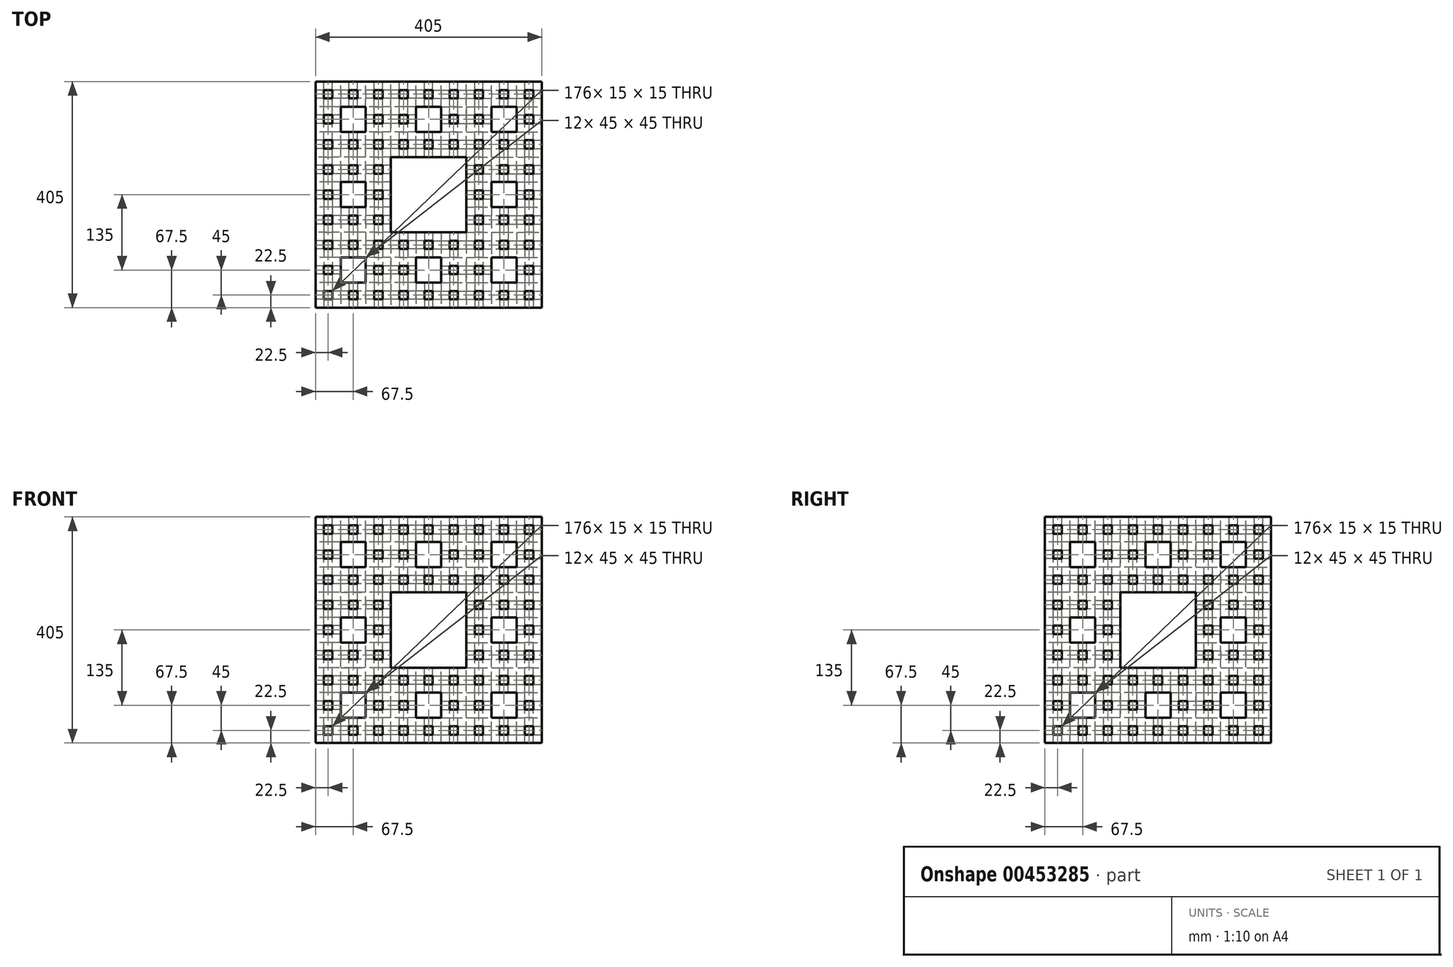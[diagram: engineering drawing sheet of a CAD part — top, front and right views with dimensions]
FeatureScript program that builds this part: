
annotation { "Feature Type Name" : "Feature", "Feature Type Description" : "" }
export const myFeature = defineFeature(function(context is Context, id is Id, definition is map)
    precondition{}
    {
        {
            var Q0;
            Q0=qCreatedBy(makeId("Top.planeOp"),FACE);
            var sketch = newSketch(context, id + "F0", { "sketchPlane" : qUnion([Q0])});
            skLineSegment(sketch, "E0.bottom", {"start": v(-202.5, 101.25) * mm, "end": v(0, 101.25) * mm});
            skLineSegment(sketch, "E0.top", {"start": v(-202.5, -101.25) * mm, "end": v(0, -101.25) * mm});
            skLineSegment(sketch, "E0.left", {"start": v(-202.5, 101.25) * mm, "end": v(-202.5, -101.25) * mm});
            skLineSegment(sketch, "E0.right", {"start": v(0, 101.25) * mm, "end": v(0, -101.25) * mm});
            skPoint(sketch, "E0.middle", {"position": v(-101.25, 0) * mm});
            skSolve(sketch);
        }
        {
            var Q0;
            Q0=makeQuery(id+"F0.imprint","IMPRINT",FACE,{"disambiguationData":[TD([[makeQuery(id+"F0.imprint","IMPRINT",EDGE,{"derivedFrom":sQuery(id+"F0.wireOp",EDGE,"E0.bottom")}),-1.0]])]});
            extrude(context, id + "F1", {"entities" : qUnion([Q0]), "depth" : 405 * mm});
        }
        {
            var Q0;
            Q0=makeQuery(id+"F1.opExtrude","SWEPT_FACE",FACE,{"disambiguationData":[OSD([sQuery(id+"F0.wireOp",EDGE,"E0.left")])]});
            var sketch = newSketch(context, id + "F2", { "sketchPlane" : qUnion([Q0])});
            skLineSegment(sketch, "E1.bottom", {"start": v(33.75, 270) * mm, "end": v(168.75, 270) * mm});
            skLineSegment(sketch, "E1.top", {"start": v(33.75, 135) * mm, "end": v(168.75, 135) * mm});
            skLineSegment(sketch, "E1.left", {"start": v(33.75, 270) * mm, "end": v(33.75, 135) * mm});
            skLineSegment(sketch, "E1.right", {"start": v(168.75, 270) * mm, "end": v(168.75, 135) * mm});
            skPoint(sketch, "E1.middle", {"position": v(101.25, 202.5) * mm});
            skSolve(sketch);
        }
        {
            var Q0;
            Q0=qSketchRegion(id+"F2",true);
            extrude(context, id + "F3", {"entities" : qUnion([Q0]), "operationType" : NewBodyOperationType.REMOVE, "oppositeDirection" : true, "depth" : 1000 * mm});
        }
        {
            var Q0;
            Q0=makeQuery(id+"F1.opExtrude","SWEPT_FACE",FACE,{"disambiguationData":[OSD([sQuery(id+"F0.wireOp",EDGE,"E0.left")])]});
            var sketch = newSketch(context, id + "F4", { "sketchPlane" : qUnion([Q0])});
            skLineSegment(sketch, "E2.bottom", {"start": v(-56.25, 360) * mm, "end": v(-11.25, 360) * mm});
            skLineSegment(sketch, "E2.top", {"start": v(-56.25, 315) * mm, "end": v(-11.25, 315) * mm});
            skLineSegment(sketch, "E2.left", {"start": v(-56.25, 360) * mm, "end": v(-56.25, 315) * mm});
            skLineSegment(sketch, "E2.right", {"start": v(-11.25, 360) * mm, "end": v(-11.25, 315) * mm});
            skPoint(sketch, "E2.middle", {"position": v(-33.75, 337.5) * mm});
            skLineSegment(sketch, "E3.bottom", {"start": v(78.75, 360) * mm, "end": v(123.75, 360) * mm});
            skLineSegment(sketch, "E3.top", {"start": v(78.75, 315) * mm, "end": v(123.75, 315) * mm});
            skLineSegment(sketch, "E3.left", {"start": v(78.75, 360) * mm, "end": v(78.75, 315) * mm});
            skLineSegment(sketch, "E3.right", {"start": v(123.75, 360) * mm, "end": v(123.75, 315) * mm});
            skPoint(sketch, "E3.middle", {"position": v(101.25, 337.5) * mm});
            skLineSegment(sketch, "E4.bottom", {"start": v(-56.25, 225) * mm, "end": v(-11.25, 225) * mm});
            skLineSegment(sketch, "E4.top", {"start": v(-56.25, 180) * mm, "end": v(-11.25, 180) * mm});
            skLineSegment(sketch, "E4.left", {"start": v(-56.25, 225) * mm, "end": v(-56.25, 180) * mm});
            skLineSegment(sketch, "E4.right", {"start": v(-11.25, 225) * mm, "end": v(-11.25, 180) * mm});
            skPoint(sketch, "E4.middle", {"position": v(-33.75, 202.5) * mm});
            skLineSegment(sketch, "E5.bottom", {"start": v(-56.25, 90) * mm, "end": v(-11.25, 90) * mm});
            skLineSegment(sketch, "E5.top", {"start": v(-56.25, 45) * mm, "end": v(-11.25, 45) * mm});
            skLineSegment(sketch, "E5.left", {"start": v(-56.25, 90) * mm, "end": v(-56.25, 45) * mm});
            skLineSegment(sketch, "E5.right", {"start": v(-11.25, 90) * mm, "end": v(-11.25, 45) * mm});
            skPoint(sketch, "E5.middle", {"position": v(-33.75, 67.5) * mm});
            skLineSegment(sketch, "E6.bottom", {"start": v(78.75, 90) * mm, "end": v(123.75, 90) * mm});
            skLineSegment(sketch, "E6.top", {"start": v(78.75, 45) * mm, "end": v(123.75, 45) * mm});
            skLineSegment(sketch, "E6.left", {"start": v(78.75, 90) * mm, "end": v(78.75, 45) * mm});
            skLineSegment(sketch, "E6.right", {"start": v(123.75, 90) * mm, "end": v(123.75, 45) * mm});
            skPoint(sketch, "E6.middle", {"position": v(101.25, 67.5) * mm});
            skSolve(sketch);
        }
        {
            var Q0;
            Q0=qSketchRegion(id+"F4",true);
            extrude(context, id + "F5", {"entities" : qUnion([Q0]), "operationType" : NewBodyOperationType.REMOVE, "oppositeDirection" : true, "depth" : 1000 * mm});
        }
        {
            var Q0;
            Q0=makeQuery(id+"F1.opExtrude","SWEPT_FACE",FACE,{"disambiguationData":[OSD([sQuery(id+"F0.wireOp",EDGE,"E0.left")])]});
            var sketch = newSketch(context, id + "F6", { "sketchPlane" : qUnion([Q0])});
            skLineSegment(sketch, "E7.bottom", {"start": v(-71.25, 390) * mm, "end": v(-86.25, 390) * mm});
            skLineSegment(sketch, "E7.top", {"start": v(-71.25, 375) * mm, "end": v(-86.25, 375) * mm});
            skLineSegment(sketch, "E7.left", {"start": v(-71.25, 390) * mm, "end": v(-71.25, 375) * mm});
            skLineSegment(sketch, "E7.right", {"start": v(-86.25, 390) * mm, "end": v(-86.25, 375) * mm});
            skPoint(sketch, "E7.middle", {"position": v(-78.75, 382.5) * mm});
            skLineSegment(sketch, "E8.bottom", {"start": v(-26.25, 390) * mm, "end": v(-41.25, 390) * mm});
            skLineSegment(sketch, "E8.top", {"start": v(-26.25, 375) * mm, "end": v(-41.25, 375) * mm});
            skLineSegment(sketch, "E8.left", {"start": v(-26.25, 390) * mm, "end": v(-26.25, 375) * mm});
            skLineSegment(sketch, "E8.right", {"start": v(-41.25, 390) * mm, "end": v(-41.25, 375) * mm});
            skPoint(sketch, "E8.middle", {"position": v(-33.75, 382.5) * mm});
            skLineSegment(sketch, "E9.bottom", {"start": v(18.75, 375) * mm, "end": v(3.75, 375) * mm});
            skLineSegment(sketch, "E9.top", {"start": v(18.75, 390) * mm, "end": v(3.75, 390) * mm});
            skLineSegment(sketch, "E9.left", {"start": v(18.75, 375) * mm, "end": v(18.75, 390) * mm});
            skLineSegment(sketch, "E9.right", {"start": v(3.75, 375) * mm, "end": v(3.75, 390) * mm});
            skPoint(sketch, "E9.middle", {"position": v(11.25, 382.5) * mm});
            skLineSegment(sketch, "E10.bottom", {"start": v(63.75, 375) * mm, "end": v(48.75, 375) * mm});
            skLineSegment(sketch, "E10.top", {"start": v(63.75, 390) * mm, "end": v(48.75, 390) * mm});
            skLineSegment(sketch, "E10.left", {"start": v(63.75, 375) * mm, "end": v(63.75, 390) * mm});
            skLineSegment(sketch, "E10.right", {"start": v(48.75, 375) * mm, "end": v(48.75, 390) * mm});
            skPoint(sketch, "E10.middle", {"position": v(56.25, 382.5) * mm});
            skLineSegment(sketch, "E11.bottom", {"start": v(93.75, 390) * mm, "end": v(108.75, 390) * mm});
            skLineSegment(sketch, "E11.top", {"start": v(93.75, 375) * mm, "end": v(108.75, 375) * mm});
            skLineSegment(sketch, "E11.left", {"start": v(93.75, 390) * mm, "end": v(93.75, 375) * mm});
            skLineSegment(sketch, "E11.right", {"start": v(108.75, 390) * mm, "end": v(108.75, 375) * mm});
            skPoint(sketch, "E11.middle", {"position": v(101.25, 382.5) * mm});
            skLineSegment(sketch, "E12.bottom", {"start": v(-86.25, 345) * mm, "end": v(-71.25, 345) * mm});
            skLineSegment(sketch, "E12.top", {"start": v(-86.25, 330) * mm, "end": v(-71.25, 330) * mm});
            skLineSegment(sketch, "E12.left", {"start": v(-86.25, 345) * mm, "end": v(-86.25, 330) * mm});
            skLineSegment(sketch, "E12.right", {"start": v(-71.25, 345) * mm, "end": v(-71.25, 330) * mm});
            skPoint(sketch, "E12.middle", {"position": v(-78.75, 337.5) * mm});
            skLineSegment(sketch, "E13.bottom", {"start": v(-86.25, 300) * mm, "end": v(-71.25, 300) * mm});
            skLineSegment(sketch, "E13.top", {"start": v(-86.25, 285) * mm, "end": v(-71.25, 285) * mm});
            skLineSegment(sketch, "E13.left", {"start": v(-86.25, 300) * mm, "end": v(-86.25, 285) * mm});
            skLineSegment(sketch, "E13.right", {"start": v(-71.25, 300) * mm, "end": v(-71.25, 285) * mm});
            skPoint(sketch, "E13.middle", {"position": v(-78.75, 292.5) * mm});
            skLineSegment(sketch, "E14.bottom", {"start": v(-86.25, 255) * mm, "end": v(-71.25, 255) * mm});
            skLineSegment(sketch, "E14.top", {"start": v(-86.25, 240) * mm, "end": v(-71.25, 240) * mm});
            skLineSegment(sketch, "E14.left", {"start": v(-86.25, 255) * mm, "end": v(-86.25, 240) * mm});
            skLineSegment(sketch, "E14.right", {"start": v(-71.25, 255) * mm, "end": v(-71.25, 240) * mm});
            skPoint(sketch, "E14.middle", {"position": v(-78.75, 247.5) * mm});
            skLineSegment(sketch, "E15.bottom", {"start": v(-86.25, 210) * mm, "end": v(-71.25, 210) * mm});
            skLineSegment(sketch, "E15.top", {"start": v(-86.25, 195) * mm, "end": v(-71.25, 195) * mm});
            skLineSegment(sketch, "E15.left", {"start": v(-86.25, 210) * mm, "end": v(-86.25, 195) * mm});
            skLineSegment(sketch, "E15.right", {"start": v(-71.25, 210) * mm, "end": v(-71.25, 195) * mm});
            skPoint(sketch, "E15.middle", {"position": v(-78.75, 202.5) * mm});
            skLineSegment(sketch, "E16.bottom", {"start": v(-86.25, 165) * mm, "end": v(-71.25, 165) * mm});
            skLineSegment(sketch, "E16.top", {"start": v(-86.25, 150) * mm, "end": v(-71.25, 150) * mm});
            skLineSegment(sketch, "E16.left", {"start": v(-86.25, 165) * mm, "end": v(-86.25, 150) * mm});
            skLineSegment(sketch, "E16.right", {"start": v(-71.25, 165) * mm, "end": v(-71.25, 150) * mm});
            skPoint(sketch, "E16.middle", {"position": v(-78.75, 157.5) * mm});
            skLineSegment(sketch, "E17.bottom", {"start": v(-86.25, 105) * mm, "end": v(-71.25, 105) * mm});
            skLineSegment(sketch, "E17.top", {"start": v(-86.25, 120) * mm, "end": v(-71.25, 120) * mm});
            skLineSegment(sketch, "E17.left", {"start": v(-86.25, 105) * mm, "end": v(-86.25, 120) * mm});
            skLineSegment(sketch, "E17.right", {"start": v(-71.25, 105) * mm, "end": v(-71.25, 120) * mm});
            skPoint(sketch, "E17.middle", {"position": v(-78.75, 112.5) * mm});
            skLineSegment(sketch, "E18.bottom", {"start": v(-86.25, 75) * mm, "end": v(-71.25, 75) * mm});
            skLineSegment(sketch, "E18.top", {"start": v(-86.25, 60) * mm, "end": v(-71.25, 60) * mm});
            skLineSegment(sketch, "E18.left", {"start": v(-86.25, 75) * mm, "end": v(-86.25, 60) * mm});
            skLineSegment(sketch, "E18.right", {"start": v(-71.25, 75) * mm, "end": v(-71.25, 60) * mm});
            skPoint(sketch, "E18.middle", {"position": v(-78.75, 67.5) * mm});
            skLineSegment(sketch, "E19.bottom", {"start": v(-86.25, 15) * mm, "end": v(-71.25, 15) * mm});
            skLineSegment(sketch, "E19.top", {"start": v(-86.25, 30) * mm, "end": v(-71.25, 30) * mm});
            skLineSegment(sketch, "E19.left", {"start": v(-86.25, 15) * mm, "end": v(-86.25, 30) * mm});
            skLineSegment(sketch, "E19.right", {"start": v(-71.25, 15) * mm, "end": v(-71.25, 30) * mm});
            skPoint(sketch, "E19.middle", {"position": v(-78.75, 22.5) * mm});
            skLineSegment(sketch, "E20", {"start": v(108.75, 390) * mm, "end": v(-86.25, 390) * mm, "construction": true});
            skLineSegment(sketch, "E21", {"start": v(-86.25, 390) * mm, "end": v(-86.25, -15.3) * mm, "construction": true});
            skLineSegment(sketch, "E22.bottom", {"start": v(-26.25, 30) * mm, "end": v(-41.25, 30) * mm});
            skLineSegment(sketch, "E22.top", {"start": v(-26.25, 15) * mm, "end": v(-41.25, 15) * mm});
            skLineSegment(sketch, "E22.left", {"start": v(-26.25, 30) * mm, "end": v(-26.25, 15) * mm});
            skLineSegment(sketch, "E22.right", {"start": v(-41.25, 30) * mm, "end": v(-41.25, 15) * mm});
            skPoint(sketch, "E22.middle", {"position": v(-33.75, 22.5) * mm});
            skLineSegment(sketch, "E23.bottom", {"start": v(18.75, 30) * mm, "end": v(3.75, 30) * mm});
            skLineSegment(sketch, "E23.top", {"start": v(18.75, 15) * mm, "end": v(3.75, 15) * mm});
            skLineSegment(sketch, "E23.left", {"start": v(18.75, 30) * mm, "end": v(18.75, 15) * mm});
            skLineSegment(sketch, "E23.right", {"start": v(3.75, 30) * mm, "end": v(3.75, 15) * mm});
            skPoint(sketch, "E23.middle", {"position": v(11.25, 22.5) * mm});
            skLineSegment(sketch, "E24.bottom", {"start": v(63.75, 30) * mm, "end": v(48.75, 30) * mm});
            skLineSegment(sketch, "E24.top", {"start": v(63.75, 15) * mm, "end": v(48.75, 15) * mm});
            skLineSegment(sketch, "E24.left", {"start": v(63.75, 30) * mm, "end": v(63.75, 15) * mm});
            skLineSegment(sketch, "E24.right", {"start": v(48.75, 30) * mm, "end": v(48.75, 15) * mm});
            skPoint(sketch, "E24.middle", {"position": v(56.25, 22.5) * mm});
            skLineSegment(sketch, "E25.bottom", {"start": v(93.75, 30) * mm, "end": v(108.75, 30) * mm});
            skLineSegment(sketch, "E25.top", {"start": v(93.75, 15) * mm, "end": v(108.75, 15) * mm});
            skLineSegment(sketch, "E25.left", {"start": v(93.75, 30) * mm, "end": v(93.75, 15) * mm});
            skLineSegment(sketch, "E25.right", {"start": v(108.75, 30) * mm, "end": v(108.75, 15) * mm});
            skPoint(sketch, "E25.middle", {"position": v(101.25, 22.5) * mm});
            skLineSegment(sketch, "E26", {"start": v(108.75, 15) * mm, "end": v(-86.25, 15) * mm, "construction": true});
            skLineSegment(sketch, "E27.bottom", {"start": v(-41.25, 285) * mm, "end": v(-26.25, 285) * mm});
            skLineSegment(sketch, "E27.top", {"start": v(-41.25, 300) * mm, "end": v(-26.25, 300) * mm});
            skLineSegment(sketch, "E27.left", {"start": v(-41.25, 285) * mm, "end": v(-41.25, 300) * mm});
            skLineSegment(sketch, "E27.right", {"start": v(-26.25, 285) * mm, "end": v(-26.25, 300) * mm});
            skPoint(sketch, "E27.middle", {"position": v(-33.75, 292.5) * mm});
            skPoint(sketch, "E27.middle.positionSnap0", {"position": v(-33.75, 315) * mm});
            skPoint(sketch, "E27.centerSnap0", {"position": v(-33.75, 315) * mm});
            skLineSegment(sketch, "E28.bottom", {"start": v(-41.25, 240) * mm, "end": v(-26.25, 240) * mm});
            skLineSegment(sketch, "E28.top", {"start": v(-41.25, 255) * mm, "end": v(-26.25, 255) * mm});
            skLineSegment(sketch, "E28.left", {"start": v(-41.25, 240) * mm, "end": v(-41.25, 255) * mm});
            skLineSegment(sketch, "E28.right", {"start": v(-26.25, 240) * mm, "end": v(-26.25, 255) * mm});
            skPoint(sketch, "E28.middle", {"position": v(-33.75, 247.5) * mm});
            skLineSegment(sketch, "E29.bottom", {"start": v(18.75, 330) * mm, "end": v(3.75, 330) * mm});
            skLineSegment(sketch, "E29.top", {"start": v(18.75, 345) * mm, "end": v(3.75, 345) * mm});
            skLineSegment(sketch, "E29.left", {"start": v(18.75, 330) * mm, "end": v(18.75, 345) * mm});
            skLineSegment(sketch, "E29.right", {"start": v(3.75, 330) * mm, "end": v(3.75, 345) * mm});
            skPoint(sketch, "E29.middle", {"position": v(11.25, 337.5) * mm});
            skPoint(sketch, "E29.middle.positionSnap0", {"position": v(-11.25, 337.5) * mm});
            skPoint(sketch, "E29.centerSnap0", {"position": v(-11.25, 337.5) * mm});
            skLineSegment(sketch, "E30.bottom", {"start": v(48.75, 330) * mm, "end": v(63.75, 330) * mm});
            skLineSegment(sketch, "E30.top", {"start": v(48.75, 345) * mm, "end": v(63.75, 345) * mm});
            skLineSegment(sketch, "E30.left", {"start": v(48.75, 330) * mm, "end": v(48.75, 345) * mm});
            skLineSegment(sketch, "E30.right", {"start": v(63.75, 330) * mm, "end": v(63.75, 345) * mm});
            skPoint(sketch, "E30.middle", {"position": v(56.25, 337.5) * mm});
            skPoint(sketch, "E30.middle.positionSnap0", {"position": v(78.75, 337.5) * mm});
            skPoint(sketch, "E30.centerSnap0", {"position": v(78.75, 337.5) * mm});
            skLineSegment(sketch, "E31.bottom", {"start": v(-41.25, 150) * mm, "end": v(-26.25, 150) * mm});
            skLineSegment(sketch, "E31.top", {"start": v(-41.25, 165) * mm, "end": v(-26.25, 165) * mm});
            skLineSegment(sketch, "E31.left", {"start": v(-41.25, 150) * mm, "end": v(-41.25, 165) * mm});
            skLineSegment(sketch, "E31.right", {"start": v(-26.25, 150) * mm, "end": v(-26.25, 165) * mm});
            skPoint(sketch, "E31.middle", {"position": v(-33.75, 157.5) * mm});
            skPoint(sketch, "E31.middle.positionSnap0", {"position": v(-33.75, 180) * mm});
            skPoint(sketch, "E31.centerSnap0", {"position": v(-33.75, 180) * mm});
            skLineSegment(sketch, "E32.bottom", {"start": v(-41.25, 120) * mm, "end": v(-26.25, 120) * mm});
            skLineSegment(sketch, "E32.top", {"start": v(-41.25, 105) * mm, "end": v(-26.25, 105) * mm});
            skLineSegment(sketch, "E32.left", {"start": v(-41.25, 120) * mm, "end": v(-41.25, 105) * mm});
            skLineSegment(sketch, "E32.right", {"start": v(-26.25, 120) * mm, "end": v(-26.25, 105) * mm});
            skPoint(sketch, "E32.middle", {"position": v(-33.75, 112.5) * mm});
            skPoint(sketch, "E32.middle.positionSnap0", {"position": v(-33.75, 90) * mm});
            skPoint(sketch, "E32.centerSnap0", {"position": v(-33.75, 90) * mm});
            skLineSegment(sketch, "E33.bottom", {"start": v(18.75, 60) * mm, "end": v(3.75, 60) * mm});
            skLineSegment(sketch, "E33.top", {"start": v(18.75, 75) * mm, "end": v(3.75, 75) * mm});
            skLineSegment(sketch, "E33.left", {"start": v(18.75, 60) * mm, "end": v(18.75, 75) * mm});
            skLineSegment(sketch, "E33.right", {"start": v(3.75, 60) * mm, "end": v(3.75, 75) * mm});
            skPoint(sketch, "E33.middle", {"position": v(11.25, 67.5) * mm});
            skPoint(sketch, "E33.middle.positionSnap0", {"position": v(11.25, 30) * mm});
            skPoint(sketch, "E33.middle.positionSnap1", {"position": v(-11.25, 67.5) * mm});
            skPoint(sketch, "E33.centerSnap0", {"position": v(11.25, 30) * mm});
            skPoint(sketch, "E33.centerSnap1", {"position": v(-11.25, 67.5) * mm});
            skLineSegment(sketch, "E34.bottom", {"start": v(48.75, 75) * mm, "end": v(63.75, 75) * mm});
            skLineSegment(sketch, "E34.top", {"start": v(48.75, 60) * mm, "end": v(63.75, 60) * mm});
            skLineSegment(sketch, "E34.left", {"start": v(48.75, 75) * mm, "end": v(48.75, 60) * mm});
            skLineSegment(sketch, "E34.right", {"start": v(63.75, 75) * mm, "end": v(63.75, 60) * mm});
            skPoint(sketch, "E34.middle", {"position": v(56.25, 67.5) * mm});
            skPoint(sketch, "E34.middle.positionSnap0", {"position": v(78.75, 67.5) * mm});
            skPoint(sketch, "E34.middle.positionSnap1", {"position": v(56.25, 30) * mm});
            skPoint(sketch, "E34.centerSnap0", {"position": v(78.75, 67.5) * mm});
            skPoint(sketch, "E34.centerSnap1", {"position": v(56.25, 30) * mm});
            skLineSegment(sketch, "E35.bottom", {"start": v(3.75, 300) * mm, "end": v(18.75, 300) * mm});
            skLineSegment(sketch, "E35.top", {"start": v(3.75, 285) * mm, "end": v(18.75, 285) * mm});
            skLineSegment(sketch, "E35.left", {"start": v(3.75, 300) * mm, "end": v(3.75, 285) * mm});
            skLineSegment(sketch, "E35.right", {"start": v(18.75, 300) * mm, "end": v(18.75, 285) * mm});
            skPoint(sketch, "E35.middle", {"position": v(11.25, 292.5) * mm});
            skPoint(sketch, "E35.middle.positionSnap0", {"position": v(-26.25, 292.5) * mm});
            skPoint(sketch, "E35.middle.positionSnap1", {"position": v(11.25, 330) * mm});
            skPoint(sketch, "E35.centerSnap0", {"position": v(-26.25, 292.5) * mm});
            skPoint(sketch, "E35.centerSnap1", {"position": v(11.25, 330) * mm});
            skLineSegment(sketch, "E36.bottom", {"start": v(48.75, 300) * mm, "end": v(63.75, 300) * mm});
            skLineSegment(sketch, "E36.top", {"start": v(48.75, 285) * mm, "end": v(63.75, 285) * mm});
            skLineSegment(sketch, "E36.left", {"start": v(48.75, 300) * mm, "end": v(48.75, 285) * mm});
            skLineSegment(sketch, "E36.right", {"start": v(63.75, 300) * mm, "end": v(63.75, 285) * mm});
            skPoint(sketch, "E36.middle", {"position": v(56.25, 292.5) * mm});
            skPoint(sketch, "E36.middle.positionSnap0", {"position": v(56.25, 330) * mm});
            skPoint(sketch, "E36.cornerSnap0", {"position": v(-33.75, 300) * mm});
            skPoint(sketch, "E36.centerSnap0", {"position": v(56.25, 330) * mm});
            skLineSegment(sketch, "E37.bottom", {"start": v(3.75, 255) * mm, "end": v(18.75, 255) * mm});
            skLineSegment(sketch, "E37.top", {"start": v(3.75, 240) * mm, "end": v(18.75, 240) * mm});
            skLineSegment(sketch, "E37.left", {"start": v(3.75, 255) * mm, "end": v(3.75, 240) * mm});
            skLineSegment(sketch, "E37.right", {"start": v(18.75, 255) * mm, "end": v(18.75, 240) * mm});
            skPoint(sketch, "E37.middle", {"position": v(11.25, 247.5) * mm});
            skPoint(sketch, "E37.middle.positionSnap0", {"position": v(-26.25, 247.5) * mm});
            skPoint(sketch, "E37.centerSnap0", {"position": v(-26.25, 247.5) * mm});
            skLineSegment(sketch, "E38.bottom", {"start": v(3.75, 195) * mm, "end": v(18.75, 195) * mm});
            skLineSegment(sketch, "E38.top", {"start": v(3.75, 210) * mm, "end": v(18.75, 210) * mm});
            skLineSegment(sketch, "E38.left", {"start": v(3.75, 195) * mm, "end": v(3.75, 210) * mm});
            skLineSegment(sketch, "E38.right", {"start": v(18.75, 195) * mm, "end": v(18.75, 210) * mm});
            skPoint(sketch, "E38.middle", {"position": v(11.25, 202.5) * mm});
            skPoint(sketch, "E38.middle.positionSnap0", {"position": v(-71.25, 202.5) * mm});
            skPoint(sketch, "E38.centerSnap0", {"position": v(-71.25, 202.5) * mm});
            skLineSegment(sketch, "E39.bottom", {"start": v(3.75, 165) * mm, "end": v(18.75, 165) * mm});
            skLineSegment(sketch, "E39.top", {"start": v(3.75, 150) * mm, "end": v(18.75, 150) * mm});
            skLineSegment(sketch, "E39.left", {"start": v(3.75, 165) * mm, "end": v(3.75, 150) * mm});
            skLineSegment(sketch, "E39.right", {"start": v(18.75, 165) * mm, "end": v(18.75, 150) * mm});
            skPoint(sketch, "E39.middle", {"position": v(11.25, 157.5) * mm});
            skPoint(sketch, "E39.middle.positionSnap0", {"position": v(-26.25, 157.5) * mm});
            skPoint(sketch, "E39.centerSnap0", {"position": v(-26.25, 157.5) * mm});
            skLineSegment(sketch, "E40.bottom", {"start": v(18.75, 120) * mm, "end": v(3.75, 120) * mm});
            skLineSegment(sketch, "E40.top", {"start": v(18.75, 105) * mm, "end": v(3.75, 105) * mm});
            skLineSegment(sketch, "E40.left", {"start": v(18.75, 120) * mm, "end": v(18.75, 105) * mm});
            skLineSegment(sketch, "E40.right", {"start": v(3.75, 120) * mm, "end": v(3.75, 105) * mm});
            skPoint(sketch, "E40.middle", {"position": v(11.25, 112.5) * mm});
            skPoint(sketch, "E40.middle.positionSnap0", {"position": v(-26.25, 112.5) * mm});
            skPoint(sketch, "E40.centerSnap0", {"position": v(-26.25, 112.5) * mm});
            skLineSegment(sketch, "E41.bottom", {"start": v(63.75, 120) * mm, "end": v(48.75, 120) * mm});
            skLineSegment(sketch, "E41.top", {"start": v(63.75, 105) * mm, "end": v(48.75, 105) * mm});
            skLineSegment(sketch, "E41.left", {"start": v(63.75, 120) * mm, "end": v(63.75, 105) * mm});
            skLineSegment(sketch, "E41.right", {"start": v(48.75, 120) * mm, "end": v(48.75, 105) * mm});
            skPoint(sketch, "E41.middle", {"position": v(56.25, 112.5) * mm});
            skLineSegment(sketch, "E42.bottom", {"start": v(93.75, 120) * mm, "end": v(108.75, 120) * mm});
            skLineSegment(sketch, "E42.top", {"start": v(93.75, 105) * mm, "end": v(108.75, 105) * mm});
            skLineSegment(sketch, "E42.left", {"start": v(93.75, 120) * mm, "end": v(93.75, 105) * mm});
            skLineSegment(sketch, "E42.right", {"start": v(108.75, 120) * mm, "end": v(108.75, 105) * mm});
            skPoint(sketch, "E42.middle", {"position": v(101.25, 112.5) * mm});
            skLineSegment(sketch, "E43.bottom", {"start": v(93.75, 300) * mm, "end": v(108.75, 300) * mm});
            skLineSegment(sketch, "E43.top", {"start": v(93.75, 285) * mm, "end": v(108.75, 285) * mm});
            skLineSegment(sketch, "E43.left", {"start": v(93.75, 300) * mm, "end": v(93.75, 285) * mm});
            skLineSegment(sketch, "E43.right", {"start": v(108.75, 300) * mm, "end": v(108.75, 285) * mm});
            skPoint(sketch, "E43.middle", {"position": v(101.25, 292.5) * mm});
            skSolve(sketch);
        }
        {
            var Q0;
            Q0=qSketchRegion(id+"F6",true);
            extrude(context, id + "F7", {"entities" : qUnion([Q0]), "operationType" : NewBodyOperationType.REMOVE, "oppositeDirection" : true, "depth" : 1000 * mm});
        }
        {
            var Q0;
            Q0=makeQuery(id+"F1.opExtrude","SWEPT_FACE",FACE,{"disambiguationData":[OSD([sQuery(id+"F0.wireOp",EDGE,"E0.bottom")])]});
            var sketch = newSketch(context, id + "F8", { "sketchPlane" : qUnion([Q0])});
            skLineSegment(sketch, "E44.bottom", {"start": v(-67.5, 270) * mm, "end": v(67.5, 270) * mm});
            skLineSegment(sketch, "E44.top", {"start": v(-67.5, 135) * mm, "end": v(67.5, 135) * mm});
            skLineSegment(sketch, "E44.left", {"start": v(-67.5, 270) * mm, "end": v(-67.5, 135) * mm});
            skLineSegment(sketch, "E44.right", {"start": v(67.5, 270) * mm, "end": v(67.5, 135) * mm});
            skPoint(sketch, "E44.middle", {"position": v(0, 202.5) * mm});
            skSolve(sketch);
        }
        {
            var Q0;
            Q0=qSketchRegion(id+"F8",true);
            extrude(context, id + "F9", {"entities" : qUnion([Q0]), "operationType" : NewBodyOperationType.REMOVE, "oppositeDirection" : true, "depth" : 1000 * mm});
        }
        {
            var Q0;
            Q0=makeQuery(id+"F1.opExtrude","SWEPT_FACE",FACE,{"disambiguationData":[OSD([sQuery(id+"F0.wireOp",EDGE,"E0.bottom")])]});
            var sketch = newSketch(context, id + "F10", { "sketchPlane" : qUnion([Q0])});
            skLineSegment(sketch, "E45.bottom", {"start": v(22.5, 360) * mm, "end": v(-22.5, 360) * mm});
            skLineSegment(sketch, "E45.top", {"start": v(22.5, 315) * mm, "end": v(-22.5, 315) * mm});
            skLineSegment(sketch, "E45.left", {"start": v(22.5, 360) * mm, "end": v(22.5, 315) * mm});
            skLineSegment(sketch, "E45.right", {"start": v(-22.5, 360) * mm, "end": v(-22.5, 315) * mm});
            skPoint(sketch, "E45.middle", {"position": v(0, 337.5) * mm});
            skLineSegment(sketch, "E46.bottom", {"start": v(157.5, 360) * mm, "end": v(112.5, 360) * mm});
            skLineSegment(sketch, "E46.top", {"start": v(157.5, 315) * mm, "end": v(112.5, 315) * mm});
            skLineSegment(sketch, "E46.left", {"start": v(157.5, 360) * mm, "end": v(157.5, 315) * mm});
            skLineSegment(sketch, "E46.right", {"start": v(112.5, 360) * mm, "end": v(112.5, 315) * mm});
            skPoint(sketch, "E46.middle", {"position": v(135, 337.5) * mm});
            skLineSegment(sketch, "E47.bottom", {"start": v(112.5, 225) * mm, "end": v(157.5, 225) * mm});
            skLineSegment(sketch, "E47.top", {"start": v(112.5, 180) * mm, "end": v(157.5, 180) * mm});
            skLineSegment(sketch, "E47.left", {"start": v(112.5, 225) * mm, "end": v(112.5, 180) * mm});
            skLineSegment(sketch, "E47.right", {"start": v(157.5, 225) * mm, "end": v(157.5, 180) * mm});
            skPoint(sketch, "E47.middle", {"position": v(135, 202.5) * mm});
            skPoint(sketch, "E47.middle.positionSnap0", {"position": v(202.5, 202.5) * mm});
            skPoint(sketch, "E47.centerSnap0", {"position": v(202.5, 202.5) * mm});
            skLineSegment(sketch, "E48.bottom", {"start": v(112.5, 90) * mm, "end": v(157.5, 90) * mm});
            skLineSegment(sketch, "E48.top", {"start": v(112.5, 45) * mm, "end": v(157.5, 45) * mm});
            skLineSegment(sketch, "E48.left", {"start": v(112.5, 90) * mm, "end": v(112.5, 45) * mm});
            skLineSegment(sketch, "E48.right", {"start": v(157.5, 90) * mm, "end": v(157.5, 45) * mm});
            skPoint(sketch, "E48.middle", {"position": v(135, 67.5) * mm});
            skLineSegment(sketch, "E49.bottom", {"start": v(22.5, 90) * mm, "end": v(-22.5, 90) * mm});
            skLineSegment(sketch, "E49.top", {"start": v(22.5, 45) * mm, "end": v(-22.5, 45) * mm});
            skLineSegment(sketch, "E49.left", {"start": v(22.5, 90) * mm, "end": v(22.5, 45) * mm});
            skLineSegment(sketch, "E49.right", {"start": v(-22.5, 90) * mm, "end": v(-22.5, 45) * mm});
            skPoint(sketch, "E49.middle", {"position": v(0, 67.5) * mm});
            skSolve(sketch);
        }
        {
            var Q0;
            Q0=qSketchRegion(id+"F10",true);
            extrude(context, id + "F11", {"entities" : qUnion([Q0]), "operationType" : NewBodyOperationType.REMOVE, "oppositeDirection" : true, "depth" : 1000 * mm});
        }
        {
            var Q0;
            Q0=makeQuery(id+"F1.opExtrude","SWEPT_FACE",FACE,{"disambiguationData":[OSD([sQuery(id+"F0.wireOp",EDGE,"E0.bottom")])]});
            var sketch = newSketch(context, id + "F12", { "sketchPlane" : qUnion([Q0])});
            skLineSegment(sketch, "E50.bottom", {"start": v(7.5, 390) * mm, "end": v(-7.5, 390) * mm});
            skLineSegment(sketch, "E50.top", {"start": v(7.5, 375) * mm, "end": v(-7.5, 375) * mm});
            skLineSegment(sketch, "E50.left", {"start": v(7.5, 390) * mm, "end": v(7.5, 375) * mm});
            skLineSegment(sketch, "E50.right", {"start": v(-7.5, 390) * mm, "end": v(-7.5, 375) * mm});
            skPoint(sketch, "E50.middle", {"position": v(0, 382.5) * mm});
            skLineSegment(sketch, "E51.bottom", {"start": v(52.5, 390) * mm, "end": v(37.5, 390) * mm});
            skLineSegment(sketch, "E51.top", {"start": v(52.5, 375) * mm, "end": v(37.5, 375) * mm});
            skLineSegment(sketch, "E51.left", {"start": v(52.5, 390) * mm, "end": v(52.5, 375) * mm});
            skLineSegment(sketch, "E51.right", {"start": v(37.5, 390) * mm, "end": v(37.5, 375) * mm});
            skPoint(sketch, "E51.middle", {"position": v(45, 382.5) * mm});
            skLineSegment(sketch, "E52.bottom", {"start": v(97.5, 390) * mm, "end": v(82.5, 390) * mm});
            skLineSegment(sketch, "E52.top", {"start": v(97.5, 375) * mm, "end": v(82.5, 375) * mm});
            skLineSegment(sketch, "E52.left", {"start": v(97.5, 390) * mm, "end": v(97.5, 375) * mm});
            skLineSegment(sketch, "E52.right", {"start": v(82.5, 390) * mm, "end": v(82.5, 375) * mm});
            skPoint(sketch, "E52.middle", {"position": v(90, 382.5) * mm});
            skLineSegment(sketch, "E53.bottom", {"start": v(142.5, 390) * mm, "end": v(127.5, 390) * mm});
            skLineSegment(sketch, "E53.top", {"start": v(142.5, 375) * mm, "end": v(127.5, 375) * mm});
            skLineSegment(sketch, "E53.left", {"start": v(142.5, 390) * mm, "end": v(142.5, 375) * mm});
            skLineSegment(sketch, "E53.right", {"start": v(127.5, 390) * mm, "end": v(127.5, 375) * mm});
            skPoint(sketch, "E53.middle", {"position": v(135, 382.5) * mm});
            skLineSegment(sketch, "E54.bottom", {"start": v(172.5, 390) * mm, "end": v(187.5, 390) * mm});
            skLineSegment(sketch, "E54.top", {"start": v(172.5, 375) * mm, "end": v(187.5, 375) * mm});
            skLineSegment(sketch, "E54.left", {"start": v(172.5, 390) * mm, "end": v(172.5, 375) * mm});
            skLineSegment(sketch, "E54.right", {"start": v(187.5, 390) * mm, "end": v(187.5, 375) * mm});
            skPoint(sketch, "E54.middle", {"position": v(180, 382.5) * mm});
            skLineSegment(sketch, "E55", {"start": v(-7.5, 390) * mm, "end": v(202.5, 390) * mm, "construction": true});
            skLineSegment(sketch, "E56.bottom", {"start": v(172.5, 345) * mm, "end": v(187.5, 345) * mm});
            skLineSegment(sketch, "E56.top", {"start": v(172.5, 330) * mm, "end": v(187.5, 330) * mm});
            skLineSegment(sketch, "E56.left", {"start": v(172.5, 345) * mm, "end": v(172.5, 330) * mm});
            skLineSegment(sketch, "E56.right", {"start": v(187.5, 345) * mm, "end": v(187.5, 330) * mm});
            skPoint(sketch, "E56.middle", {"position": v(180, 337.5) * mm});
            skPoint(sketch, "E56.middle.positionSnap0", {"position": v(157.5, 337.5) * mm});
            skPoint(sketch, "E56.middle.positionSnap1", {"position": v(180, 375) * mm});
            skPoint(sketch, "E56.centerSnap0", {"position": v(157.5, 337.5) * mm});
            skPoint(sketch, "E56.centerSnap1", {"position": v(180, 375) * mm});
            skLineSegment(sketch, "E57.bottom", {"start": v(172.5, 210) * mm, "end": v(187.5, 210) * mm});
            skLineSegment(sketch, "E57.top", {"start": v(172.5, 195) * mm, "end": v(187.5, 195) * mm});
            skLineSegment(sketch, "E57.left", {"start": v(172.5, 210) * mm, "end": v(172.5, 195) * mm});
            skLineSegment(sketch, "E57.right", {"start": v(187.5, 210) * mm, "end": v(187.5, 195) * mm});
            skPoint(sketch, "E57.middle", {"position": v(180, 202.5) * mm});
            skPoint(sketch, "E57.middle.positionSnap0", {"position": v(180, 330) * mm});
            skPoint(sketch, "E57.middle.positionSnap1", {"position": v(157.5, 202.5) * mm});
            skPoint(sketch, "E57.centerSnap0", {"position": v(180, 330) * mm});
            skPoint(sketch, "E57.centerSnap1", {"position": v(157.5, 202.5) * mm});
            skLineSegment(sketch, "E58.bottom", {"start": v(172.5, 75) * mm, "end": v(187.5, 75) * mm});
            skLineSegment(sketch, "E58.top", {"start": v(172.5, 60) * mm, "end": v(187.5, 60) * mm});
            skLineSegment(sketch, "E58.left", {"start": v(172.5, 75) * mm, "end": v(172.5, 60) * mm});
            skLineSegment(sketch, "E58.right", {"start": v(187.5, 75) * mm, "end": v(187.5, 60) * mm});
            skPoint(sketch, "E58.middle", {"position": v(180, 67.5) * mm});
            skPoint(sketch, "E58.middle.positionSnap0", {"position": v(157.5, 67.5) * mm});
            skPoint(sketch, "E58.centerSnap0", {"position": v(157.5, 67.5) * mm});
            skLineSegment(sketch, "E59.bottom", {"start": v(172.5, 30) * mm, "end": v(187.5, 30) * mm});
            skLineSegment(sketch, "E59.top", {"start": v(172.5, 15) * mm, "end": v(187.5, 15) * mm});
            skLineSegment(sketch, "E59.left", {"start": v(172.5, 30) * mm, "end": v(172.5, 15) * mm});
            skLineSegment(sketch, "E59.right", {"start": v(187.5, 30) * mm, "end": v(187.5, 15) * mm});
            skPoint(sketch, "E59.middle", {"position": v(180, 22.5) * mm});
            skLineSegment(sketch, "E60.bottom", {"start": v(187.5, 285) * mm, "end": v(172.5, 285) * mm});
            skLineSegment(sketch, "E60.top", {"start": v(187.5, 300) * mm, "end": v(172.5, 300) * mm});
            skLineSegment(sketch, "E60.left", {"start": v(187.5, 285) * mm, "end": v(187.5, 300) * mm});
            skLineSegment(sketch, "E60.right", {"start": v(172.5, 285) * mm, "end": v(172.5, 300) * mm});
            skPoint(sketch, "E60.middle", {"position": v(180, 292.5) * mm});
            skLineSegment(sketch, "E61.bottom", {"start": v(187.5, 240) * mm, "end": v(172.5, 240) * mm});
            skLineSegment(sketch, "E61.top", {"start": v(187.5, 255) * mm, "end": v(172.5, 255) * mm});
            skLineSegment(sketch, "E61.left", {"start": v(187.5, 240) * mm, "end": v(187.5, 255) * mm});
            skLineSegment(sketch, "E61.right", {"start": v(172.5, 240) * mm, "end": v(172.5, 255) * mm});
            skPoint(sketch, "E61.middle", {"position": v(180, 247.5) * mm});
            skLineSegment(sketch, "E62.bottom", {"start": v(187.5, 150) * mm, "end": v(172.5, 150) * mm});
            skLineSegment(sketch, "E62.top", {"start": v(187.5, 165) * mm, "end": v(172.5, 165) * mm});
            skLineSegment(sketch, "E62.left", {"start": v(187.5, 150) * mm, "end": v(187.5, 165) * mm});
            skLineSegment(sketch, "E62.right", {"start": v(172.5, 150) * mm, "end": v(172.5, 165) * mm});
            skPoint(sketch, "E62.middle", {"position": v(180, 157.5) * mm});
            skLineSegment(sketch, "E63.bottom", {"start": v(187.5, 120) * mm, "end": v(172.5, 120) * mm});
            skLineSegment(sketch, "E63.top", {"start": v(187.5, 105) * mm, "end": v(172.5, 105) * mm});
            skLineSegment(sketch, "E63.left", {"start": v(187.5, 120) * mm, "end": v(187.5, 105) * mm});
            skLineSegment(sketch, "E63.right", {"start": v(172.5, 120) * mm, "end": v(172.5, 105) * mm});
            skPoint(sketch, "E63.middle", {"position": v(180, 112.5) * mm});
            skLineSegment(sketch, "E64", {"start": v(187.5, 390) * mm, "end": v(187.5, -8.34) * mm, "construction": true});
            skLineSegment(sketch, "E65.bottom", {"start": v(127.5, 285) * mm, "end": v(142.5, 285) * mm});
            skLineSegment(sketch, "E65.top", {"start": v(127.5, 300) * mm, "end": v(142.5, 300) * mm});
            skLineSegment(sketch, "E65.left", {"start": v(127.5, 285) * mm, "end": v(127.5, 300) * mm});
            skLineSegment(sketch, "E65.right", {"start": v(142.5, 285) * mm, "end": v(142.5, 300) * mm});
            skPoint(sketch, "E65.middle", {"position": v(135, 292.5) * mm});
            skPoint(sketch, "E65.middle.positionSnap0", {"position": v(172.5, 292.5) * mm});
            skPoint(sketch, "E65.middle.positionSnap1", {"position": v(135, 315) * mm});
            skPoint(sketch, "E65.centerSnap0", {"position": v(172.5, 292.5) * mm});
            skPoint(sketch, "E65.centerSnap1", {"position": v(135, 315) * mm});
            skLineSegment(sketch, "E66.bottom", {"start": v(127.5, 255) * mm, "end": v(142.5, 255) * mm});
            skLineSegment(sketch, "E66.top", {"start": v(127.5, 240) * mm, "end": v(142.5, 240) * mm});
            skLineSegment(sketch, "E66.left", {"start": v(127.5, 255) * mm, "end": v(127.5, 240) * mm});
            skLineSegment(sketch, "E66.right", {"start": v(142.5, 255) * mm, "end": v(142.5, 240) * mm});
            skPoint(sketch, "E66.middle", {"position": v(135, 247.5) * mm});
            skPoint(sketch, "E66.middle.positionSnap0", {"position": v(135, 285) * mm});
            skPoint(sketch, "E66.middle.positionSnap1", {"position": v(172.5, 247.5) * mm});
            skPoint(sketch, "E66.centerSnap0", {"position": v(135, 285) * mm});
            skPoint(sketch, "E66.centerSnap1", {"position": v(172.5, 247.5) * mm});
            skLineSegment(sketch, "E67.bottom", {"start": v(127.5, 150) * mm, "end": v(142.5, 150) * mm});
            skLineSegment(sketch, "E67.top", {"start": v(127.5, 165) * mm, "end": v(142.5, 165) * mm});
            skLineSegment(sketch, "E67.left", {"start": v(127.5, 150) * mm, "end": v(127.5, 165) * mm});
            skLineSegment(sketch, "E67.right", {"start": v(142.5, 150) * mm, "end": v(142.5, 165) * mm});
            skPoint(sketch, "E67.middle", {"position": v(135, 157.5) * mm});
            skPoint(sketch, "E67.middle.positionSnap0", {"position": v(172.5, 157.5) * mm});
            skPoint(sketch, "E67.middle.positionSnap1", {"position": v(135, 180) * mm});
            skPoint(sketch, "E67.centerSnap0", {"position": v(172.5, 157.5) * mm});
            skPoint(sketch, "E67.centerSnap1", {"position": v(135, 180) * mm});
            skLineSegment(sketch, "E68.bottom", {"start": v(127.5, 120) * mm, "end": v(142.5, 120) * mm});
            skLineSegment(sketch, "E68.top", {"start": v(127.5, 105) * mm, "end": v(142.5, 105) * mm});
            skLineSegment(sketch, "E68.left", {"start": v(127.5, 120) * mm, "end": v(127.5, 105) * mm});
            skLineSegment(sketch, "E68.right", {"start": v(142.5, 120) * mm, "end": v(142.5, 105) * mm});
            skPoint(sketch, "E68.middle", {"position": v(135, 112.5) * mm});
            skPoint(sketch, "E68.middle.positionSnap0", {"position": v(135, 150) * mm});
            skPoint(sketch, "E68.middle.positionSnap1", {"position": v(172.5, 112.5) * mm});
            skPoint(sketch, "E68.centerSnap0", {"position": v(135, 150) * mm});
            skPoint(sketch, "E68.centerSnap1", {"position": v(172.5, 112.5) * mm});
            skLineSegment(sketch, "E69.bottom", {"start": v(142.5, 30) * mm, "end": v(127.5, 30) * mm});
            skLineSegment(sketch, "E69.top", {"start": v(142.5, 15) * mm, "end": v(127.5, 15) * mm});
            skLineSegment(sketch, "E69.left", {"start": v(142.5, 30) * mm, "end": v(142.5, 15) * mm});
            skLineSegment(sketch, "E69.right", {"start": v(127.5, 30) * mm, "end": v(127.5, 15) * mm});
            skPoint(sketch, "E69.middle", {"position": v(135, 22.5) * mm});
            skPoint(sketch, "E69.middle.positionSnap0", {"position": v(172.5, 22.5) * mm});
            skPoint(sketch, "E69.middle.positionSnap1", {"position": v(135, 45) * mm});
            skPoint(sketch, "E69.centerSnap0", {"position": v(172.5, 22.5) * mm});
            skPoint(sketch, "E69.centerSnap1", {"position": v(135, 45) * mm});
            skLineSegment(sketch, "E70.bottom", {"start": v(82.5, 330) * mm, "end": v(97.5, 330) * mm});
            skLineSegment(sketch, "E70.top", {"start": v(82.5, 345) * mm, "end": v(97.5, 345) * mm});
            skLineSegment(sketch, "E70.left", {"start": v(82.5, 330) * mm, "end": v(82.5, 345) * mm});
            skLineSegment(sketch, "E70.right", {"start": v(97.5, 330) * mm, "end": v(97.5, 345) * mm});
            skPoint(sketch, "E70.middle", {"position": v(90, 337.5) * mm});
            skPoint(sketch, "E70.middle.positionSnap0", {"position": v(112.5, 337.5) * mm});
            skPoint(sketch, "E70.middle.positionSnap1", {"position": v(90, 375) * mm});
            skPoint(sketch, "E70.centerSnap0", {"position": v(112.5, 337.5) * mm});
            skPoint(sketch, "E70.centerSnap1", {"position": v(90, 375) * mm});
            skLineSegment(sketch, "E71.bottom", {"start": v(37.5, 330) * mm, "end": v(52.5, 330) * mm});
            skLineSegment(sketch, "E71.top", {"start": v(37.5, 345) * mm, "end": v(52.5, 345) * mm});
            skLineSegment(sketch, "E71.left", {"start": v(37.5, 330) * mm, "end": v(37.5, 345) * mm});
            skLineSegment(sketch, "E71.right", {"start": v(52.5, 330) * mm, "end": v(52.5, 345) * mm});
            skPoint(sketch, "E71.middle", {"position": v(45, 337.5) * mm});
            skPoint(sketch, "E71.middle.positionSnap0", {"position": v(82.5, 337.5) * mm});
            skPoint(sketch, "E71.middle.positionSnap1", {"position": v(45, 375) * mm});
            skPoint(sketch, "E71.centerSnap0", {"position": v(82.5, 337.5) * mm});
            skPoint(sketch, "E71.centerSnap1", {"position": v(45, 375) * mm});
            skLineSegment(sketch, "E72.bottom", {"start": v(82.5, 285) * mm, "end": v(97.5, 285) * mm});
            skLineSegment(sketch, "E72.top", {"start": v(82.5, 300) * mm, "end": v(97.5, 300) * mm});
            skLineSegment(sketch, "E72.left", {"start": v(82.5, 285) * mm, "end": v(82.5, 300) * mm});
            skLineSegment(sketch, "E72.right", {"start": v(97.5, 285) * mm, "end": v(97.5, 300) * mm});
            skPoint(sketch, "E72.middle", {"position": v(90, 292.5) * mm});
            skPoint(sketch, "E72.middle.positionSnap0", {"position": v(127.5, 292.5) * mm});
            skPoint(sketch, "E72.middle.positionSnap1", {"position": v(90, 330) * mm});
            skPoint(sketch, "E72.centerSnap0", {"position": v(127.5, 292.5) * mm});
            skPoint(sketch, "E72.centerSnap1", {"position": v(90, 330) * mm});
            skLineSegment(sketch, "E73.bottom", {"start": v(52.5, 300) * mm, "end": v(37.5, 300) * mm});
            skLineSegment(sketch, "E73.top", {"start": v(52.5, 285) * mm, "end": v(37.5, 285) * mm});
            skLineSegment(sketch, "E73.left", {"start": v(52.5, 300) * mm, "end": v(52.5, 285) * mm});
            skLineSegment(sketch, "E73.right", {"start": v(37.5, 300) * mm, "end": v(37.5, 285) * mm});
            skPoint(sketch, "E73.middle", {"position": v(45, 292.5) * mm});
            skPoint(sketch, "E73.middle.positionSnap0", {"position": v(82.5, 292.5) * mm});
            skPoint(sketch, "E73.middle.positionSnap1", {"position": v(45, 330) * mm});
            skPoint(sketch, "E73.centerSnap0", {"position": v(82.5, 292.5) * mm});
            skPoint(sketch, "E73.centerSnap1", {"position": v(45, 330) * mm});
            skLineSegment(sketch, "E74.bottom", {"start": v(7.5, 300) * mm, "end": v(-7.5, 300) * mm});
            skLineSegment(sketch, "E74.top", {"start": v(7.5, 285) * mm, "end": v(-7.5, 285) * mm});
            skLineSegment(sketch, "E74.left", {"start": v(7.5, 300) * mm, "end": v(7.5, 285) * mm});
            skLineSegment(sketch, "E74.right", {"start": v(-7.5, 300) * mm, "end": v(-7.5, 285) * mm});
            skPoint(sketch, "E74.middle", {"position": v(0, 292.5) * mm});
            skLineSegment(sketch, "E75.bottom", {"start": v(97.5, 255) * mm, "end": v(82.5, 255) * mm});
            skLineSegment(sketch, "E75.top", {"start": v(97.5, 240) * mm, "end": v(82.5, 240) * mm});
            skLineSegment(sketch, "E75.left", {"start": v(97.5, 255) * mm, "end": v(97.5, 240) * mm});
            skLineSegment(sketch, "E75.right", {"start": v(82.5, 255) * mm, "end": v(82.5, 240) * mm});
            skPoint(sketch, "E75.middle", {"position": v(90, 247.5) * mm});
            skPoint(sketch, "E75.middle.positionSnap0", {"position": v(127.5, 247.5) * mm});
            skPoint(sketch, "E75.middle.positionSnap1", {"position": v(90, 285) * mm});
            skPoint(sketch, "E75.centerSnap0", {"position": v(127.5, 247.5) * mm});
            skPoint(sketch, "E75.centerSnap1", {"position": v(90, 285) * mm});
            skLineSegment(sketch, "E76.bottom", {"start": v(97.5, 210) * mm, "end": v(82.5, 210) * mm});
            skLineSegment(sketch, "E76.top", {"start": v(97.5, 195) * mm, "end": v(82.5, 195) * mm});
            skLineSegment(sketch, "E76.left", {"start": v(97.5, 210) * mm, "end": v(97.5, 195) * mm});
            skLineSegment(sketch, "E76.right", {"start": v(82.5, 210) * mm, "end": v(82.5, 195) * mm});
            skPoint(sketch, "E76.middle", {"position": v(90, 202.5) * mm});
            skPoint(sketch, "E76.middle.positionSnap0", {"position": v(90, 240) * mm});
            skPoint(sketch, "E76.centerSnap0", {"position": v(90, 240) * mm});
            skLineSegment(sketch, "E77.bottom", {"start": v(97.5, 165) * mm, "end": v(82.5, 165) * mm});
            skLineSegment(sketch, "E77.top", {"start": v(97.5, 150) * mm, "end": v(82.5, 150) * mm});
            skLineSegment(sketch, "E77.left", {"start": v(97.5, 165) * mm, "end": v(97.5, 150) * mm});
            skLineSegment(sketch, "E77.right", {"start": v(82.5, 165) * mm, "end": v(82.5, 150) * mm});
            skPoint(sketch, "E77.middle", {"position": v(90, 157.5) * mm});
            skPoint(sketch, "E77.middle.positionSnap0", {"position": v(127.5, 157.5) * mm});
            skPoint(sketch, "E77.centerSnap0", {"position": v(127.5, 157.5) * mm});
            skLineSegment(sketch, "E78.bottom", {"start": v(97.5, 120) * mm, "end": v(82.5, 120) * mm});
            skLineSegment(sketch, "E78.top", {"start": v(97.5, 105) * mm, "end": v(82.5, 105) * mm});
            skLineSegment(sketch, "E78.left", {"start": v(97.5, 120) * mm, "end": v(97.5, 105) * mm});
            skLineSegment(sketch, "E78.right", {"start": v(82.5, 120) * mm, "end": v(82.5, 105) * mm});
            skPoint(sketch, "E78.middle", {"position": v(90, 112.5) * mm});
            skPoint(sketch, "E78.middle.positionSnap0", {"position": v(127.5, 112.5) * mm});
            skPoint(sketch, "E78.centerSnap0", {"position": v(127.5, 112.5) * mm});
            skLineSegment(sketch, "E79.bottom", {"start": v(97.5, 75) * mm, "end": v(82.5, 75) * mm});
            skLineSegment(sketch, "E79.top", {"start": v(97.5, 60) * mm, "end": v(82.5, 60) * mm});
            skLineSegment(sketch, "E79.left", {"start": v(97.5, 75) * mm, "end": v(97.5, 60) * mm});
            skLineSegment(sketch, "E79.right", {"start": v(82.5, 75) * mm, "end": v(82.5, 60) * mm});
            skPoint(sketch, "E79.middle", {"position": v(90, 67.5) * mm});
            skPoint(sketch, "E79.middle.positionSnap0", {"position": v(90, 105) * mm});
            skPoint(sketch, "E79.centerSnap0", {"position": v(90, 105) * mm});
            skLineSegment(sketch, "E80.bottom", {"start": v(97.5, 30) * mm, "end": v(82.5, 30) * mm});
            skLineSegment(sketch, "E80.top", {"start": v(97.5, 15) * mm, "end": v(82.5, 15) * mm});
            skLineSegment(sketch, "E80.left", {"start": v(97.5, 30) * mm, "end": v(97.5, 15) * mm});
            skLineSegment(sketch, "E80.right", {"start": v(82.5, 30) * mm, "end": v(82.5, 15) * mm});
            skPoint(sketch, "E80.middle", {"position": v(90, 22.5) * mm});
            skPoint(sketch, "E80.middle.positionSnap0", {"position": v(127.5, 22.5) * mm});
            skPoint(sketch, "E80.centerSnap0", {"position": v(127.5, 22.5) * mm});
            skLineSegment(sketch, "E81.bottom", {"start": v(7.5, 120) * mm, "end": v(-7.5, 120) * mm});
            skLineSegment(sketch, "E81.top", {"start": v(7.5, 105) * mm, "end": v(-7.5, 105) * mm});
            skLineSegment(sketch, "E81.left", {"start": v(7.5, 120) * mm, "end": v(7.5, 105) * mm});
            skLineSegment(sketch, "E81.right", {"start": v(-7.5, 120) * mm, "end": v(-7.5, 105) * mm});
            skPoint(sketch, "E81.middle", {"position": v(0, 112.5) * mm});
            skLineSegment(sketch, "E82.bottom", {"start": v(37.5, 105) * mm, "end": v(52.5, 105) * mm});
            skLineSegment(sketch, "E82.top", {"start": v(37.5, 120) * mm, "end": v(52.5, 120) * mm});
            skLineSegment(sketch, "E82.left", {"start": v(37.5, 105) * mm, "end": v(37.5, 120) * mm});
            skLineSegment(sketch, "E82.right", {"start": v(52.5, 105) * mm, "end": v(52.5, 120) * mm});
            skPoint(sketch, "E82.middle", {"position": v(45, 112.5) * mm});
            skPoint(sketch, "E82.middle.positionSnap0", {"position": v(82.5, 112.5) * mm});
            skPoint(sketch, "E82.middle.positionSnap1", {"position": v(45, 285) * mm});
            skPoint(sketch, "E82.cornerSnap0", {"position": v(37.5, 292.5) * mm});
            skPoint(sketch, "E82.centerSnap0", {"position": v(82.5, 112.5) * mm});
            skPoint(sketch, "E82.centerSnap1", {"position": v(45, 285) * mm});
            skLineSegment(sketch, "E83.bottom", {"start": v(52.5, 75) * mm, "end": v(37.5, 75) * mm});
            skLineSegment(sketch, "E83.top", {"start": v(52.5, 60) * mm, "end": v(37.5, 60) * mm});
            skLineSegment(sketch, "E83.left", {"start": v(52.5, 75) * mm, "end": v(52.5, 60) * mm});
            skLineSegment(sketch, "E83.right", {"start": v(37.5, 75) * mm, "end": v(37.5, 60) * mm});
            skPoint(sketch, "E83.middle", {"position": v(45, 67.5) * mm});
            skPoint(sketch, "E83.middle.positionSnap0", {"position": v(45, 105) * mm});
            skPoint(sketch, "E83.middle.positionSnap1", {"position": v(82.5, 67.5) * mm});
            skPoint(sketch, "E83.centerSnap0", {"position": v(45, 105) * mm});
            skPoint(sketch, "E83.centerSnap1", {"position": v(82.5, 67.5) * mm});
            skLineSegment(sketch, "E84.bottom", {"start": v(7.5, 30) * mm, "end": v(-7.5, 30) * mm});
            skLineSegment(sketch, "E84.top", {"start": v(7.5, 15) * mm, "end": v(-7.5, 15) * mm});
            skLineSegment(sketch, "E84.left", {"start": v(7.5, 30) * mm, "end": v(7.5, 15) * mm});
            skLineSegment(sketch, "E84.right", {"start": v(-7.5, 30) * mm, "end": v(-7.5, 15) * mm});
            skPoint(sketch, "E84.middle", {"position": v(0, 22.5) * mm});
            skLineSegment(sketch, "E85.bottom", {"start": v(52.5, 30) * mm, "end": v(37.5, 30) * mm});
            skLineSegment(sketch, "E85.top", {"start": v(52.5, 15) * mm, "end": v(37.5, 15) * mm});
            skLineSegment(sketch, "E85.left", {"start": v(52.5, 30) * mm, "end": v(52.5, 15) * mm});
            skLineSegment(sketch, "E85.right", {"start": v(37.5, 30) * mm, "end": v(37.5, 15) * mm});
            skPoint(sketch, "E85.middle", {"position": v(45, 22.5) * mm});
            skPoint(sketch, "E85.middle.positionSnap0", {"position": v(82.5, 22.5) * mm});
            skPoint(sketch, "E85.middle.positionSnap1", {"position": v(45, 60) * mm});
            skPoint(sketch, "E85.centerSnap0", {"position": v(82.5, 22.5) * mm});
            skPoint(sketch, "E85.centerSnap1", {"position": v(45, 60) * mm});
            skSolve(sketch);
        }
        {
            var Q0;
            Q0=qSketchRegion(id+"F12",true);
            extrude(context, id + "F13", {"entities" : qUnion([Q0]), "operationType" : NewBodyOperationType.REMOVE, "oppositeDirection" : true, "depth" : 1000 * mm});
        }
        {
            var Q0;
            Q0=makeQuery(id+"F1.opExtrude","SWEPT_BODY",BODY,{"disambiguationData":[OSD([sQuery(id+"F0.wireOp",EDGE,"E0.bottom"),sQuery(id+"F0.wireOp",EDGE,"E0.top"),sQuery(id+"F0.wireOp",EDGE,"E0.left"),sQuery(id+"F0.wireOp",EDGE,"E0.right")])]});
            var Q1;
            {var subQ7=makeQuery(id+"F3.boolean.opBoolean","COPY",FACE,{"derivedFrom":makeQuery(id+"F3.opExtrude","SWEPT_FACE",FACE,{"disambiguationData":[OSD([sQuery(id+"F2.wireOp",EDGE,"E1.bottom")])]})});var subQ27=sQuery(id+"F0.wireOp",EDGE,"E0.right");Q1=makeQuery(id+"F13.boolean.opBoolean","SPLIT",FACE,{"disambiguationData":[TD([subQ7])],"derivedFrom":makeQuery(id+"F11.boolean.opBoolean","SPLIT",FACE,{"disambiguationData":[TD([subQ7])],"derivedFrom":makeQuery(id+"F9.boolean.opBoolean","SPLIT",FACE,{"disambiguationData":[TD([subQ7])],"derivedFrom":makeQuery(id+"F1.opExtrude","SWEPT_FACE",FACE,{"disambiguationData":[OSD([subQ27])]})})})});}
            mirror(context, id + "F14", {"operationType" : NewBodyOperationType.ADD, "entities" : qUnion([Q0]), "mirrorPlane" : qUnion([Q1])});
        }
        {
            var Q0;
            {var subQ0=makeQuery(id+"F1.opExtrude","CAP_FACE",FACE,{"disambiguationData":[OSD([sQuery(id+"F0.wireOp",EDGE,"E0.bottom"),sQuery(id+"F0.wireOp",EDGE,"E0.top"),sQuery(id+"F0.wireOp",EDGE,"E0.left"),sQuery(id+"F0.wireOp",EDGE,"E0.right")])],"isStart":false});Q0=makeQuery(id+"F14.boolean.opBoolean","MERGE",FACE,{"derivedFrom":[subQ0,makeQuery(id+"F14.opPattern","COPY",FACE,{"derivedFrom":subQ0,"instanceName":"1"})]});}
            var sketch = newSketch(context, id + "F15", { "sketchPlane" : qUnion([Q0])});
            skLineSegment(sketch, "E86.bottom", {"start": v(-67.5, -33.75) * mm, "end": v(67.5, -33.75) * mm});
            skLineSegment(sketch, "E86.top", {"start": v(-67.5, -168.75) * mm, "end": v(67.5, -168.75) * mm});
            skLineSegment(sketch, "E86.left", {"start": v(-67.5, -33.75) * mm, "end": v(-67.5, -168.75) * mm});
            skLineSegment(sketch, "E86.right", {"start": v(67.5, -33.75) * mm, "end": v(67.5, -168.75) * mm});
            skPoint(sketch, "E86.middle", {"position": v(0, -101.25) * mm});
            skSolve(sketch);
        }
        {
            var Q0;
            Q0=qSketchRegion(id+"F15",true);
            extrude(context, id + "F16", {"entities" : qUnion([Q0]), "operationType" : NewBodyOperationType.REMOVE, "oppositeDirection" : true, "depth" : 1000 * mm});
        }
        {
            var Q0;
            {var subQ0=makeQuery(id+"F1.opExtrude","CAP_FACE",FACE,{"disambiguationData":[OSD([sQuery(id+"F0.wireOp",EDGE,"E0.bottom"),sQuery(id+"F0.wireOp",EDGE,"E0.top"),sQuery(id+"F0.wireOp",EDGE,"E0.left"),sQuery(id+"F0.wireOp",EDGE,"E0.right")])],"isStart":false});Q0=makeQuery(id+"F14.boolean.opBoolean","MERGE",FACE,{"derivedFrom":[subQ0,makeQuery(id+"F14.opPattern","COPY",FACE,{"derivedFrom":subQ0,"instanceName":"1"})]});}
            var sketch = newSketch(context, id + "F17", { "sketchPlane" : qUnion([Q0])});
            skLineSegment(sketch, "E87.bottom", {"start": v(-112.5, -78.75) * mm, "end": v(-157.5, -78.75) * mm});
            skLineSegment(sketch, "E87.top", {"start": v(-112.5, -123.75) * mm, "end": v(-157.5, -123.75) * mm});
            skLineSegment(sketch, "E87.left", {"start": v(-112.5, -78.75) * mm, "end": v(-112.5, -123.75) * mm});
            skLineSegment(sketch, "E87.right", {"start": v(-157.5, -78.75) * mm, "end": v(-157.5, -123.75) * mm});
            skPoint(sketch, "E87.middle", {"position": v(-135, -101.25) * mm});
            skLineSegment(sketch, "E88.bottom", {"start": v(157.5, -78.75) * mm, "end": v(112.5, -78.75) * mm});
            skLineSegment(sketch, "E88.top", {"start": v(157.5, -123.75) * mm, "end": v(112.5, -123.75) * mm});
            skLineSegment(sketch, "E88.left", {"start": v(157.5, -78.75) * mm, "end": v(157.5, -123.75) * mm});
            skLineSegment(sketch, "E88.right", {"start": v(112.5, -78.75) * mm, "end": v(112.5, -123.75) * mm});
            skPoint(sketch, "E88.middle", {"position": v(135, -101.25) * mm});
            skLineSegment(sketch, "E89.bottom", {"start": v(-22.5, 56.25) * mm, "end": v(22.5, 56.25) * mm});
            skLineSegment(sketch, "E89.top", {"start": v(-22.5, 11.25) * mm, "end": v(22.5, 11.25) * mm});
            skLineSegment(sketch, "E89.left", {"start": v(-22.5, 56.25) * mm, "end": v(-22.5, 11.25) * mm});
            skLineSegment(sketch, "E89.right", {"start": v(22.5, 56.25) * mm, "end": v(22.5, 11.25) * mm});
            skPoint(sketch, "E89.middle", {"position": v(0, 33.75) * mm});
            skLineSegment(sketch, "E90.bottom", {"start": v(-112.5, 56.25) * mm, "end": v(-157.5, 56.25) * mm});
            skLineSegment(sketch, "E90.top", {"start": v(-112.5, 11.25) * mm, "end": v(-157.5, 11.25) * mm});
            skLineSegment(sketch, "E90.left", {"start": v(-112.5, 56.25) * mm, "end": v(-112.5, 11.25) * mm});
            skLineSegment(sketch, "E90.right", {"start": v(-157.5, 56.25) * mm, "end": v(-157.5, 11.25) * mm});
            skPoint(sketch, "E90.middle", {"position": v(-135, 33.75) * mm});
            skPoint(sketch, "E91.middle", {"position": v(-135, -25) * mm});
            skLineSegment(sketch, "E92.bottom", {"start": v(112.5, 56.25) * mm, "end": v(157.5, 56.25) * mm});
            skLineSegment(sketch, "E92.top", {"start": v(112.5, 11.25) * mm, "end": v(157.5, 11.25) * mm});
            skLineSegment(sketch, "E92.left", {"start": v(112.5, 56.25) * mm, "end": v(112.5, 11.25) * mm});
            skLineSegment(sketch, "E92.right", {"start": v(157.5, 56.25) * mm, "end": v(157.5, 11.25) * mm});
            skPoint(sketch, "E92.middle", {"position": v(135, 33.75) * mm});
            skPoint(sketch, "E93.middle", {"position": v(135, -26.25) * mm});
            skSolve(sketch);
        }
        {
            var Q0;
            Q0=qSketchRegion(id+"F17",true);
            extrude(context, id + "F18", {"entities" : qUnion([Q0]), "operationType" : NewBodyOperationType.REMOVE, "oppositeDirection" : true, "depth" : 1000 * mm});
        }
        {
            var Q0;
            {var subQ0=makeQuery(id+"F1.opExtrude","CAP_FACE",FACE,{"disambiguationData":[OSD([sQuery(id+"F0.wireOp",EDGE,"E0.bottom"),sQuery(id+"F0.wireOp",EDGE,"E0.top"),sQuery(id+"F0.wireOp",EDGE,"E0.left"),sQuery(id+"F0.wireOp",EDGE,"E0.right")])],"isStart":false});Q0=makeQuery(id+"F14.boolean.opBoolean","MERGE",FACE,{"derivedFrom":[subQ0,makeQuery(id+"F14.opPattern","COPY",FACE,{"derivedFrom":subQ0,"instanceName":"1"})]});}
            var sketch = newSketch(context, id + "F19", { "sketchPlane" : qUnion([Q0])});
            skLineSegment(sketch, "E94.bottom", {"start": v(-187.5, -93.75) * mm, "end": v(-172.5, -93.75) * mm});
            skLineSegment(sketch, "E94.top", {"start": v(-187.5, -108.75) * mm, "end": v(-172.5, -108.75) * mm});
            skLineSegment(sketch, "E94.left", {"start": v(-187.5, -93.75) * mm, "end": v(-187.5, -108.75) * mm});
            skLineSegment(sketch, "E94.right", {"start": v(-172.5, -93.75) * mm, "end": v(-172.5, -108.75) * mm});
            skPoint(sketch, "E94.middle", {"position": v(-180, -101.25) * mm});
            skLineSegment(sketch, "E95.bottom", {"start": v(-187.5, 41.25) * mm, "end": v(-172.5, 41.25) * mm});
            skLineSegment(sketch, "E95.top", {"start": v(-187.5, 26.25) * mm, "end": v(-172.5, 26.25) * mm});
            skLineSegment(sketch, "E95.left", {"start": v(-187.5, 41.25) * mm, "end": v(-187.5, 26.25) * mm});
            skLineSegment(sketch, "E95.right", {"start": v(-172.5, 41.25) * mm, "end": v(-172.5, 26.25) * mm});
            skPoint(sketch, "E95.middle", {"position": v(-180, 33.75) * mm});
            skPoint(sketch, "E95.middle.positionSnap0", {"position": v(-157.5, 33.75) * mm});
            skPoint(sketch, "E95.centerSnap0", {"position": v(-157.5, 33.75) * mm});
            skLineSegment(sketch, "E96.bottom", {"start": v(-187.5, 86.25) * mm, "end": v(-172.5, 86.25) * mm});
            skLineSegment(sketch, "E96.top", {"start": v(-187.5, 71.25) * mm, "end": v(-172.5, 71.25) * mm});
            skLineSegment(sketch, "E96.left", {"start": v(-187.5, 86.25) * mm, "end": v(-187.5, 71.25) * mm});
            skLineSegment(sketch, "E96.right", {"start": v(-172.5, 86.25) * mm, "end": v(-172.5, 71.25) * mm});
            skPoint(sketch, "E96.middle", {"position": v(-180, 78.75) * mm});
            skLineSegment(sketch, "E97.bottom", {"start": v(-187.5, -3.75) * mm, "end": v(-172.5, -3.75) * mm});
            skLineSegment(sketch, "E97.top", {"start": v(-187.5, -18.75) * mm, "end": v(-172.5, -18.75) * mm});
            skLineSegment(sketch, "E97.left", {"start": v(-187.5, -3.75) * mm, "end": v(-187.5, -18.75) * mm});
            skLineSegment(sketch, "E97.right", {"start": v(-172.5, -3.75) * mm, "end": v(-172.5, -18.75) * mm});
            skPoint(sketch, "E97.middle", {"position": v(-180, -11.25) * mm});
            skLineSegment(sketch, "E98.bottom", {"start": v(-187.5, -48.75) * mm, "end": v(-172.5, -48.75) * mm});
            skLineSegment(sketch, "E98.top", {"start": v(-187.5, -63.75) * mm, "end": v(-172.5, -63.75) * mm});
            skLineSegment(sketch, "E98.left", {"start": v(-187.5, -48.75) * mm, "end": v(-187.5, -63.75) * mm});
            skLineSegment(sketch, "E98.right", {"start": v(-172.5, -48.75) * mm, "end": v(-172.5, -63.75) * mm});
            skPoint(sketch, "E98.middle", {"position": v(-180, -56.25) * mm});
            skLineSegment(sketch, "E99.bottom", {"start": v(172.5, 71.25) * mm, "end": v(187.5, 71.25) * mm});
            skLineSegment(sketch, "E99.top", {"start": v(172.5, 86.25) * mm, "end": v(187.5, 86.25) * mm});
            skLineSegment(sketch, "E99.left", {"start": v(172.5, 71.25) * mm, "end": v(172.5, 86.25) * mm});
            skLineSegment(sketch, "E99.right", {"start": v(187.5, 71.25) * mm, "end": v(187.5, 86.25) * mm});
            skPoint(sketch, "E99.middle", {"position": v(180, 78.75) * mm});
            skLineSegment(sketch, "E100.bottom", {"start": v(172.5, 26.25) * mm, "end": v(187.5, 26.25) * mm});
            skLineSegment(sketch, "E100.top", {"start": v(172.5, 41.25) * mm, "end": v(187.5, 41.25) * mm});
            skLineSegment(sketch, "E100.left", {"start": v(172.5, 26.25) * mm, "end": v(172.5, 41.25) * mm});
            skLineSegment(sketch, "E100.right", {"start": v(187.5, 26.25) * mm, "end": v(187.5, 41.25) * mm});
            skPoint(sketch, "E100.middle", {"position": v(180, 33.75) * mm});
            skLineSegment(sketch, "E101.bottom", {"start": v(172.5, -18.75) * mm, "end": v(187.5, -18.75) * mm});
            skLineSegment(sketch, "E101.top", {"start": v(172.5, -3.75) * mm, "end": v(187.5, -3.75) * mm});
            skLineSegment(sketch, "E101.left", {"start": v(172.5, -18.75) * mm, "end": v(172.5, -3.75) * mm});
            skLineSegment(sketch, "E101.right", {"start": v(187.5, -18.75) * mm, "end": v(187.5, -3.75) * mm});
            skPoint(sketch, "E101.middle", {"position": v(180, -11.25) * mm});
            skLineSegment(sketch, "E102.bottom", {"start": v(172.5, -48.75) * mm, "end": v(187.5, -48.75) * mm});
            skLineSegment(sketch, "E102.top", {"start": v(172.5, -63.75) * mm, "end": v(187.5, -63.75) * mm});
            skLineSegment(sketch, "E102.left", {"start": v(172.5, -48.75) * mm, "end": v(172.5, -63.75) * mm});
            skLineSegment(sketch, "E102.right", {"start": v(187.5, -48.75) * mm, "end": v(187.5, -63.75) * mm});
            skPoint(sketch, "E102.middle", {"position": v(180, -56.25) * mm});
            skLineSegment(sketch, "E103.bottom", {"start": v(172.5, -93.75) * mm, "end": v(187.5, -93.75) * mm});
            skLineSegment(sketch, "E103.top", {"start": v(172.5, -108.75) * mm, "end": v(187.5, -108.75) * mm});
            skLineSegment(sketch, "E103.left", {"start": v(172.5, -93.75) * mm, "end": v(172.5, -108.75) * mm});
            skLineSegment(sketch, "E103.right", {"start": v(187.5, -93.75) * mm, "end": v(187.5, -108.75) * mm});
            skPoint(sketch, "E103.middle", {"position": v(180, -101.25) * mm});
            skLineSegment(sketch, "E104.bottom", {"start": v(127.5, 86.25) * mm, "end": v(142.5, 86.25) * mm});
            skLineSegment(sketch, "E104.top", {"start": v(127.5, 71.25) * mm, "end": v(142.5, 71.25) * mm});
            skLineSegment(sketch, "E104.left", {"start": v(127.5, 86.25) * mm, "end": v(127.5, 71.25) * mm});
            skLineSegment(sketch, "E104.right", {"start": v(142.5, 86.25) * mm, "end": v(142.5, 71.25) * mm});
            skPoint(sketch, "E104.middle", {"position": v(135, 78.75) * mm});
            skLineSegment(sketch, "E105.bottom", {"start": v(82.5, 86.25) * mm, "end": v(97.5, 86.25) * mm});
            skLineSegment(sketch, "E105.top", {"start": v(82.5, 71.25) * mm, "end": v(97.5, 71.25) * mm});
            skLineSegment(sketch, "E105.left", {"start": v(82.5, 86.25) * mm, "end": v(82.5, 71.25) * mm});
            skLineSegment(sketch, "E105.right", {"start": v(97.5, 86.25) * mm, "end": v(97.5, 71.25) * mm});
            skPoint(sketch, "E105.middle", {"position": v(90, 78.75) * mm});
            skLineSegment(sketch, "E106.bottom", {"start": v(37.5, 86.25) * mm, "end": v(52.5, 86.25) * mm});
            skLineSegment(sketch, "E106.top", {"start": v(37.5, 71.25) * mm, "end": v(52.5, 71.25) * mm});
            skLineSegment(sketch, "E106.left", {"start": v(37.5, 86.25) * mm, "end": v(37.5, 71.25) * mm});
            skLineSegment(sketch, "E106.right", {"start": v(52.5, 86.25) * mm, "end": v(52.5, 71.25) * mm});
            skPoint(sketch, "E106.middle", {"position": v(45, 78.75) * mm});
            skLineSegment(sketch, "E107.bottom", {"start": v(-7.5, 86.25) * mm, "end": v(7.5, 86.25) * mm});
            skLineSegment(sketch, "E107.top", {"start": v(-7.5, 71.25) * mm, "end": v(7.5, 71.25) * mm});
            skLineSegment(sketch, "E107.left", {"start": v(-7.5, 86.25) * mm, "end": v(-7.5, 71.25) * mm});
            skLineSegment(sketch, "E107.right", {"start": v(7.5, 86.25) * mm, "end": v(7.5, 71.25) * mm});
            skPoint(sketch, "E107.middle", {"position": v(0, 78.75) * mm});
            skLineSegment(sketch, "E108.bottom", {"start": v(-52.5, 86.25) * mm, "end": v(-37.5, 86.25) * mm});
            skLineSegment(sketch, "E108.top", {"start": v(-52.5, 71.25) * mm, "end": v(-37.5, 71.25) * mm});
            skLineSegment(sketch, "E108.left", {"start": v(-52.5, 86.25) * mm, "end": v(-52.5, 71.25) * mm});
            skLineSegment(sketch, "E108.right", {"start": v(-37.5, 86.25) * mm, "end": v(-37.5, 71.25) * mm});
            skPoint(sketch, "E108.middle", {"position": v(-45, 78.75) * mm});
            skLineSegment(sketch, "E109.bottom", {"start": v(-97.5, 86.25) * mm, "end": v(-82.5, 86.25) * mm});
            skLineSegment(sketch, "E109.top", {"start": v(-97.5, 71.25) * mm, "end": v(-82.5, 71.25) * mm});
            skLineSegment(sketch, "E109.left", {"start": v(-97.5, 86.25) * mm, "end": v(-97.5, 71.25) * mm});
            skLineSegment(sketch, "E109.right", {"start": v(-82.5, 86.25) * mm, "end": v(-82.5, 71.25) * mm});
            skPoint(sketch, "E109.middle", {"position": v(-90, 78.75) * mm});
            skLineSegment(sketch, "E110.bottom", {"start": v(-142.5, 86.25) * mm, "end": v(-127.5, 86.25) * mm});
            skLineSegment(sketch, "E110.top", {"start": v(-142.5, 71.25) * mm, "end": v(-127.5, 71.25) * mm});
            skLineSegment(sketch, "E110.left", {"start": v(-142.5, 86.25) * mm, "end": v(-142.5, 71.25) * mm});
            skLineSegment(sketch, "E110.right", {"start": v(-127.5, 86.25) * mm, "end": v(-127.5, 71.25) * mm});
            skPoint(sketch, "E110.middle", {"position": v(-135, 78.75) * mm});
            skLineSegment(sketch, "E111", {"start": v(-172.5, 86.25) * mm, "end": v(206.92, 86.25) * mm, "construction": true});
            skLineSegment(sketch, "E112", {"start": v(-187.5, -108.75) * mm, "end": v(-187.5, 125) * mm, "construction": true});
            skLineSegment(sketch, "E113", {"start": v(187.5, 86.25) * mm, "end": v(187.5, -113.42) * mm, "construction": true});
            skLineSegment(sketch, "E114.bottom", {"start": v(-97.5, 41.25) * mm, "end": v(-82.5, 41.25) * mm});
            skLineSegment(sketch, "E114.top", {"start": v(-97.5, 26.25) * mm, "end": v(-82.5, 26.25) * mm});
            skLineSegment(sketch, "E114.left", {"start": v(-97.5, 41.25) * mm, "end": v(-97.5, 26.25) * mm});
            skLineSegment(sketch, "E114.right", {"start": v(-82.5, 41.25) * mm, "end": v(-82.5, 26.25) * mm});
            skPoint(sketch, "E114.middle", {"position": v(-90, 33.75) * mm});
            skPoint(sketch, "E114.middle.positionSnap0", {"position": v(-112.5, 33.75) * mm});
            skPoint(sketch, "E114.middle.positionSnap1", {"position": v(-90, 71.25) * mm});
            skPoint(sketch, "E114.centerSnap0", {"position": v(-112.5, 33.75) * mm});
            skPoint(sketch, "E114.centerSnap1", {"position": v(-90, 71.25) * mm});
            skLineSegment(sketch, "E115.bottom", {"start": v(-37.5, 41.25) * mm, "end": v(-52.5, 41.25) * mm});
            skLineSegment(sketch, "E115.top", {"start": v(-37.5, 26.25) * mm, "end": v(-52.5, 26.25) * mm});
            skLineSegment(sketch, "E115.left", {"start": v(-37.5, 41.25) * mm, "end": v(-37.5, 26.25) * mm});
            skLineSegment(sketch, "E115.right", {"start": v(-52.5, 41.25) * mm, "end": v(-52.5, 26.25) * mm});
            skPoint(sketch, "E115.middle", {"position": v(-45, 33.75) * mm});
            skPoint(sketch, "E115.middle.positionSnap0", {"position": v(-22.5, 33.75) * mm});
            skPoint(sketch, "E115.middle.positionSnap1", {"position": v(-45, 71.25) * mm});
            skPoint(sketch, "E115.centerSnap0", {"position": v(-22.5, 33.75) * mm});
            skPoint(sketch, "E115.centerSnap1", {"position": v(-45, 71.25) * mm});
            skLineSegment(sketch, "E116.bottom", {"start": v(52.5, 41.25) * mm, "end": v(37.5, 41.25) * mm});
            skLineSegment(sketch, "E116.top", {"start": v(52.5, 26.25) * mm, "end": v(37.5, 26.25) * mm});
            skLineSegment(sketch, "E116.left", {"start": v(52.5, 41.25) * mm, "end": v(52.5, 26.25) * mm});
            skLineSegment(sketch, "E116.right", {"start": v(37.5, 41.25) * mm, "end": v(37.5, 26.25) * mm});
            skPoint(sketch, "E116.middle", {"position": v(45, 33.75) * mm});
            skPoint(sketch, "E116.middle.positionSnap0", {"position": v(172.5, 33.75) * mm});
            skPoint(sketch, "E116.middle.positionSnap1", {"position": v(45, 71.25) * mm});
            skPoint(sketch, "E116.centerSnap0", {"position": v(172.5, 33.75) * mm});
            skPoint(sketch, "E116.centerSnap1", {"position": v(45, 71.25) * mm});
            skLineSegment(sketch, "E117.bottom", {"start": v(97.5, 41.25) * mm, "end": v(82.5, 41.25) * mm});
            skLineSegment(sketch, "E117.top", {"start": v(97.5, 26.25) * mm, "end": v(82.5, 26.25) * mm});
            skLineSegment(sketch, "E117.left", {"start": v(97.5, 41.25) * mm, "end": v(97.5, 26.25) * mm});
            skLineSegment(sketch, "E117.right", {"start": v(82.5, 41.25) * mm, "end": v(82.5, 26.25) * mm});
            skPoint(sketch, "E117.middle", {"position": v(90, 33.75) * mm});
            skPoint(sketch, "E117.middle.positionSnap0", {"position": v(52.5, 33.75) * mm});
            skPoint(sketch, "E117.middle.positionSnap1", {"position": v(90, 71.25) * mm});
            skPoint(sketch, "E117.centerSnap0", {"position": v(52.5, 33.75) * mm});
            skPoint(sketch, "E117.centerSnap1", {"position": v(90, 71.25) * mm});
            skLineSegment(sketch, "E118.bottom", {"start": v(-142.5, -3.75) * mm, "end": v(-127.5, -3.75) * mm});
            skLineSegment(sketch, "E118.top", {"start": v(-142.5, -18.75) * mm, "end": v(-127.5, -18.75) * mm});
            skLineSegment(sketch, "E118.left", {"start": v(-142.5, -3.75) * mm, "end": v(-142.5, -18.75) * mm});
            skLineSegment(sketch, "E118.right", {"start": v(-127.5, -3.75) * mm, "end": v(-127.5, -18.75) * mm});
            skPoint(sketch, "E118.middle", {"position": v(-135, -11.25) * mm});
            skPoint(sketch, "E118.middle.positionSnap0", {"position": v(-135, 71.25) * mm});
            skPoint(sketch, "E118.middle.positionSnap1", {"position": v(-172.5, -11.25) * mm});
            skPoint(sketch, "E118.centerSnap0", {"position": v(-135, 71.25) * mm});
            skPoint(sketch, "E118.centerSnap1", {"position": v(-172.5, -11.25) * mm});
            skLineSegment(sketch, "E119.bottom", {"start": v(-97.5, -3.75) * mm, "end": v(-82.5, -3.75) * mm});
            skLineSegment(sketch, "E119.top", {"start": v(-97.5, -18.75) * mm, "end": v(-82.5, -18.75) * mm});
            skLineSegment(sketch, "E119.left", {"start": v(-97.5, -3.75) * mm, "end": v(-97.5, -18.75) * mm});
            skLineSegment(sketch, "E119.right", {"start": v(-82.5, -3.75) * mm, "end": v(-82.5, -18.75) * mm});
            skPoint(sketch, "E119.middle", {"position": v(-90, -11.25) * mm});
            skPoint(sketch, "E119.middle.positionSnap0", {"position": v(-127.5, -11.25) * mm});
            skPoint(sketch, "E119.middle.positionSnap1", {"position": v(-90, 26.25) * mm});
            skPoint(sketch, "E119.centerSnap0", {"position": v(-127.5, -11.25) * mm});
            skPoint(sketch, "E119.centerSnap1", {"position": v(-90, 26.25) * mm});
            skLineSegment(sketch, "E120.bottom", {"start": v(-52.5, -3.75) * mm, "end": v(-37.5, -3.75) * mm});
            skLineSegment(sketch, "E120.top", {"start": v(-52.5, -18.75) * mm, "end": v(-37.5, -18.75) * mm});
            skLineSegment(sketch, "E120.left", {"start": v(-52.5, -3.75) * mm, "end": v(-52.5, -18.75) * mm});
            skLineSegment(sketch, "E120.right", {"start": v(-37.5, -3.75) * mm, "end": v(-37.5, -18.75) * mm});
            skPoint(sketch, "E120.middle", {"position": v(-45, -11.25) * mm});
            skPoint(sketch, "E120.middle.positionSnap0", {"position": v(-45, 26.25) * mm});
            skPoint(sketch, "E120.middle.positionSnap1", {"position": v(-82.5, -11.25) * mm});
            skPoint(sketch, "E120.centerSnap0", {"position": v(-45, 26.25) * mm});
            skPoint(sketch, "E120.centerSnap1", {"position": v(-82.5, -11.25) * mm});
            skLineSegment(sketch, "E121.bottom", {"start": v(-7.5, -3.75) * mm, "end": v(7.5, -3.75) * mm});
            skLineSegment(sketch, "E121.top", {"start": v(-7.5, -18.75) * mm, "end": v(7.5, -18.75) * mm});
            skLineSegment(sketch, "E121.left", {"start": v(-7.5, -3.75) * mm, "end": v(-7.5, -18.75) * mm});
            skLineSegment(sketch, "E121.right", {"start": v(7.5, -3.75) * mm, "end": v(7.5, -18.75) * mm});
            skPoint(sketch, "E121.middle", {"position": v(0, -11.25) * mm});
            skPoint(sketch, "E121.middle.positionSnap0", {"position": v(-37.5, -11.25) * mm});
            skPoint(sketch, "E121.middle.positionSnap1", {"position": v(0, 71.25) * mm});
            skPoint(sketch, "E121.centerSnap0", {"position": v(-37.5, -11.25) * mm});
            skPoint(sketch, "E121.centerSnap1", {"position": v(0, 71.25) * mm});
            skLineSegment(sketch, "E122.bottom", {"start": v(37.5, -3.75) * mm, "end": v(52.5, -3.75) * mm});
            skLineSegment(sketch, "E122.top", {"start": v(37.5, -18.75) * mm, "end": v(52.5, -18.75) * mm});
            skLineSegment(sketch, "E122.left", {"start": v(37.5, -3.75) * mm, "end": v(37.5, -18.75) * mm});
            skLineSegment(sketch, "E122.right", {"start": v(52.5, -3.75) * mm, "end": v(52.5, -18.75) * mm});
            skPoint(sketch, "E122.middle", {"position": v(45, -11.25) * mm});
            skPoint(sketch, "E122.middle.positionSnap0", {"position": v(45, 26.25) * mm});
            skPoint(sketch, "E122.centerSnap0", {"position": v(45, 26.25) * mm});
            skLineSegment(sketch, "E123.bottom", {"start": v(82.5, -3.75) * mm, "end": v(97.5, -3.75) * mm});
            skLineSegment(sketch, "E123.top", {"start": v(82.5, -18.75) * mm, "end": v(97.5, -18.75) * mm});
            skLineSegment(sketch, "E123.left", {"start": v(82.5, -3.75) * mm, "end": v(82.5, -18.75) * mm});
            skLineSegment(sketch, "E123.right", {"start": v(97.5, -3.75) * mm, "end": v(97.5, -18.75) * mm});
            skPoint(sketch, "E123.middle", {"position": v(90, -11.25) * mm});
            skPoint(sketch, "E123.middle.positionSnap0", {"position": v(52.5, -11.25) * mm});
            skPoint(sketch, "E123.middle.positionSnap1", {"position": v(90, 26.25) * mm});
            skPoint(sketch, "E123.centerSnap0", {"position": v(52.5, -11.25) * mm});
            skPoint(sketch, "E123.centerSnap1", {"position": v(90, 26.25) * mm});
            skLineSegment(sketch, "E124.bottom", {"start": v(127.5, -3.75) * mm, "end": v(142.5, -3.75) * mm});
            skLineSegment(sketch, "E124.top", {"start": v(127.5, -18.75) * mm, "end": v(142.5, -18.75) * mm});
            skLineSegment(sketch, "E124.left", {"start": v(127.5, -3.75) * mm, "end": v(127.5, -18.75) * mm});
            skLineSegment(sketch, "E124.right", {"start": v(142.5, -3.75) * mm, "end": v(142.5, -18.75) * mm});
            skPoint(sketch, "E124.middle", {"position": v(135, -11.25) * mm});
            skPoint(sketch, "E124.middle.positionSnap0", {"position": v(97.5, -11.25) * mm});
            skPoint(sketch, "E124.middle.positionSnap1", {"position": v(135, 71.25) * mm});
            skPoint(sketch, "E124.centerSnap0", {"position": v(97.5, -11.25) * mm});
            skPoint(sketch, "E124.centerSnap1", {"position": v(135, 71.25) * mm});
            skLineSegment(sketch, "E125.bottom", {"start": v(82.5, -48.75) * mm, "end": v(97.5, -48.75) * mm});
            skLineSegment(sketch, "E125.top", {"start": v(82.5, -63.75) * mm, "end": v(97.5, -63.75) * mm});
            skLineSegment(sketch, "E125.left", {"start": v(82.5, -48.75) * mm, "end": v(82.5, -63.75) * mm});
            skLineSegment(sketch, "E125.right", {"start": v(97.5, -48.75) * mm, "end": v(97.5, -63.75) * mm});
            skPoint(sketch, "E125.middle", {"position": v(90, -56.25) * mm});
            skPoint(sketch, "E125.middle.positionSnap0", {"position": v(172.5, -56.25) * mm});
            skPoint(sketch, "E125.middle.positionSnap1", {"position": v(90, -18.75) * mm});
            skPoint(sketch, "E125.centerSnap0", {"position": v(172.5, -56.25) * mm});
            skPoint(sketch, "E125.centerSnap1", {"position": v(90, -18.75) * mm});
            skLineSegment(sketch, "E126.bottom", {"start": v(142.5, -48.75) * mm, "end": v(127.5, -48.75) * mm});
            skLineSegment(sketch, "E126.top", {"start": v(142.5, -63.75) * mm, "end": v(127.5, -63.75) * mm});
            skLineSegment(sketch, "E126.left", {"start": v(142.5, -48.75) * mm, "end": v(142.5, -63.75) * mm});
            skLineSegment(sketch, "E126.right", {"start": v(127.5, -48.75) * mm, "end": v(127.5, -63.75) * mm});
            skPoint(sketch, "E126.middle", {"position": v(135, -56.25) * mm});
            skPoint(sketch, "E126.middle.positionSnap0", {"position": v(135, -18.75) * mm});
            skPoint(sketch, "E126.centerSnap0", {"position": v(135, -18.75) * mm});
            skLineSegment(sketch, "E127.bottom", {"start": v(97.5, -93.75) * mm, "end": v(82.5, -93.75) * mm});
            skLineSegment(sketch, "E127.top", {"start": v(97.5, -108.75) * mm, "end": v(82.5, -108.75) * mm});
            skLineSegment(sketch, "E127.left", {"start": v(97.5, -93.75) * mm, "end": v(97.5, -108.75) * mm});
            skLineSegment(sketch, "E127.right", {"start": v(82.5, -93.75) * mm, "end": v(82.5, -108.75) * mm});
            skPoint(sketch, "E127.middle", {"position": v(90, -101.25) * mm});
            skLineSegment(sketch, "E128.bottom", {"start": v(-142.5, -48.75) * mm, "end": v(-127.5, -48.75) * mm});
            skLineSegment(sketch, "E128.top", {"start": v(-142.5, -63.75) * mm, "end": v(-127.5, -63.75) * mm});
            skLineSegment(sketch, "E128.left", {"start": v(-142.5, -48.75) * mm, "end": v(-142.5, -63.75) * mm});
            skLineSegment(sketch, "E128.right", {"start": v(-127.5, -48.75) * mm, "end": v(-127.5, -63.75) * mm});
            skPoint(sketch, "E128.middle", {"position": v(-135, -56.25) * mm});
            skPoint(sketch, "E128.middle.positionSnap0", {"position": v(-135, -18.75) * mm});
            skPoint(sketch, "E128.centerSnap0", {"position": v(-135, -18.75) * mm});
            skLineSegment(sketch, "E129.bottom", {"start": v(-97.5, -63.75) * mm, "end": v(-82.5, -63.75) * mm});
            skLineSegment(sketch, "E129.top", {"start": v(-97.5, -48.75) * mm, "end": v(-82.5, -48.75) * mm});
            skLineSegment(sketch, "E129.left", {"start": v(-97.5, -63.75) * mm, "end": v(-97.5, -48.75) * mm});
            skLineSegment(sketch, "E129.right", {"start": v(-82.5, -63.75) * mm, "end": v(-82.5, -48.75) * mm});
            skPoint(sketch, "E129.middle", {"position": v(-90, -56.25) * mm});
            skPoint(sketch, "E129.middle.positionSnap0", {"position": v(-127.5, -56.25) * mm});
            skPoint(sketch, "E129.middle.positionSnap1", {"position": v(-90, -18.75) * mm});
            skPoint(sketch, "E129.centerSnap0", {"position": v(-127.5, -56.25) * mm});
            skPoint(sketch, "E129.centerSnap1", {"position": v(-90, -18.75) * mm});
            skLineSegment(sketch, "E130.bottom", {"start": v(-97.5, -93.75) * mm, "end": v(-82.5, -93.75) * mm});
            skLineSegment(sketch, "E130.top", {"start": v(-97.5, -108.75) * mm, "end": v(-82.5, -108.75) * mm});
            skLineSegment(sketch, "E130.left", {"start": v(-97.5, -93.75) * mm, "end": v(-97.5, -108.75) * mm});
            skLineSegment(sketch, "E130.right", {"start": v(-82.5, -93.75) * mm, "end": v(-82.5, -108.75) * mm});
            skPoint(sketch, "E130.middle", {"position": v(-90, -101.25) * mm});
            skSolve(sketch);
        }
        {
            var Q0;
            Q0=qSketchRegion(id+"F19",true);
            extrude(context, id + "F20", {"entities" : qUnion([Q0]), "operationType" : NewBodyOperationType.REMOVE, "oppositeDirection" : true, "depth" : 1000 * mm});
        }
        {
            var Q0;
            Q0=makeQuery(id+"F1.opExtrude","SWEPT_BODY",BODY,{"disambiguationData":[OSD([sQuery(id+"F0.wireOp",EDGE,"E0.bottom"),sQuery(id+"F0.wireOp",EDGE,"E0.top"),sQuery(id+"F0.wireOp",EDGE,"E0.left"),sQuery(id+"F0.wireOp",EDGE,"E0.right")])]});
            var Q1;
            {var subQ4=makeQuery(id+"F7.opExtrude","SWEPT_FACE",FACE,{"disambiguationData":[OSD([sQuery(id+"F6.wireOp",EDGE,"E11.bottom")])]});var subQ14=makeQuery(id+"F5.opExtrude","SWEPT_FACE",FACE,{"disambiguationData":[OSD([sQuery(id+"F4.wireOp",EDGE,"E3.bottom")])]});var subQ33=sQuery(id+"F0.wireOp",EDGE,"E0.top");var subQ34=makeQuery(id+"F1.opExtrude","SWEPT_FACE",FACE,{"disambiguationData":[OSD([subQ33])]});var subQ44=sQuery(id+"F0.wireOp",EDGE,"E0.left");var subQ48=makeQuery(id+"F1.opExtrude","SWEPT_FACE",FACE,{"disambiguationData":[OSD([subQ44])]});var subQ50=makeQuery(id+"F3.opExtrude","SWEPT_FACE",FACE,{"disambiguationData":[OSD([sQuery(id+"F2.wireOp",EDGE,"E1.bottom")])]});var subQ51=makeQuery(id+"F3.boolean.opBoolean","SPLIT",FACE,{"disambiguationData":[TD([subQ50])],"derivedFrom":subQ34});var subQ52=makeQuery(id+"F5.boolean.opBoolean","SPLIT",FACE,{"disambiguationData":[TD([subQ14])],"derivedFrom":subQ51});var subQ53=makeQuery(id+"F7.boolean.opBoolean","SPLIT",FACE,{"disambiguationData":[TD([subQ4])],"derivedFrom":subQ52});var subQ54=makeQuery(id+"F14.opPattern","COPY",FACE,{"derivedFrom":subQ53,"instanceName":"1"});var subQ57=makeQuery(id+"F18.opExtrude","SWEPT_FACE",FACE,{"disambiguationData":[OSD([sQuery(id+"F17.wireOp",EDGE,"E87.left")])]});Q1=makeQuery(id+"F20.boolean.opBoolean","SPLIT",FACE,{"disambiguationData":[TD([makeQuery(id+"F20.opExtrude","SWEPT_FACE",FACE,{"disambiguationData":[OSD([sQuery(id+"F19.wireOp",EDGE,"E130.left")])]})])],"derivedFrom":makeQuery(id+"F18.boolean.opBoolean","SPLIT",FACE,{"disambiguationData":[TD([subQ57])],"derivedFrom":makeQuery(id+"F16.boolean.opBoolean","SPLIT",FACE,{"disambiguationData":[TD([subQ48])],"derivedFrom":makeQuery(id+"F14.boolean.opBoolean","MERGE",FACE,{"derivedFrom":[subQ53,subQ54]})})})});}
            mirror(context, id + "F21", {"operationType" : NewBodyOperationType.ADD, "entities" : qUnion([Q0]), "mirrorPlane" : qUnion([Q1])});
        }
    });
